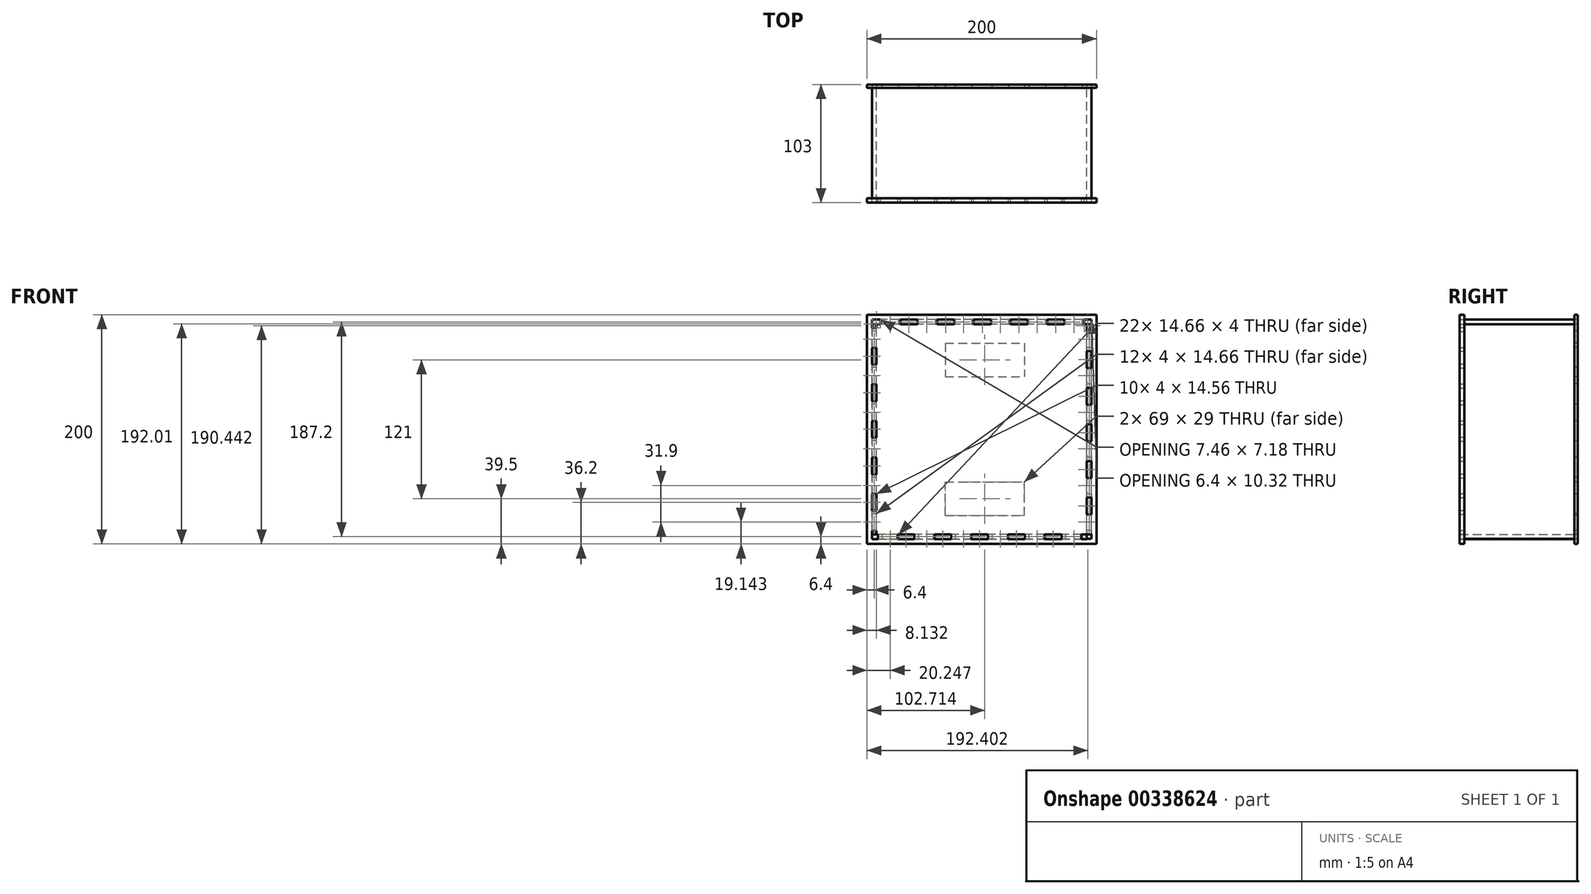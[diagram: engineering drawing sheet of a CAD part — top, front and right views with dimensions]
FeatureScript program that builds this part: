
annotation { "Feature Type Name" : "Feature", "Feature Type Description" : "" }
export const myFeature = defineFeature(function(context is Context, id is Id, definition is map)
    precondition{}
    {
        {
            var Q0;
            Q0=qCreatedBy(makeId("Front.planeOp"),FACE);
            var sketch = newSketch(context, id + "F0", { "sketchPlane" : qUnion([Q0])});
            skLineSegment(sketch, "E0.bottom", {"start": v(-100, 100) * mm, "end": v(100, 100) * mm});
            skLineSegment(sketch, "E0.top", {"start": v(-100, -100) * mm, "end": v(100, -100) * mm});
            skLineSegment(sketch, "E0.left", {"start": v(-100, 100) * mm, "end": v(-100, -100) * mm});
            skLineSegment(sketch, "E0.right", {"start": v(100, 100) * mm, "end": v(100, -100) * mm});
            skPoint(sketch, "E0.middle", {"position": v(0, 0) * mm});
            skSolve(sketch);
        }
        {
            var Q0;
            Q0 = qSketchRegion(id + "F0", true);
            extrude(context, id + "F1", {"entities" : qUnion([Q0]), "depth" : 3 * mm, "offsetDistance" : 25 * mm});
        }
        {
            var Q0;
            Q0=makeQuery(id+"F1.opExtrude","CAP_FACE",FACE,{"disambiguationData":[OSD([sQuery(id+"F0.wireOp",EDGE,"E0.bottom"),sQuery(id+"F0.wireOp",EDGE,"E0.top"),sQuery(id+"F0.wireOp",EDGE,"E0.left"),sQuery(id+"F0.wireOp",EDGE,"E0.right")])],"isStart":false});
            var sketch = newSketch(context, id + "F2", { "sketchPlane" : qUnion([Q0])});
            skLineSegment(sketch, "E1.0", {"start": v(-91.6, 91.6) * mm, "end": v(91.6, 91.6) * mm, "construction": true});
            skLineSegment(sketch, "E1.1", {"start": v(-91.6, 91.6) * mm, "end": v(-91.6, -91.6) * mm, "construction": true});
            skLineSegment(sketch, "E1.2", {"start": v(-91.6, -91.6) * mm, "end": v(91.6, -91.6) * mm, "construction": true});
            skLineSegment(sketch, "E1.3", {"start": v(91.6, 91.6) * mm, "end": v(91.6, -91.6) * mm, "construction": true});
            skLineSegment(sketch, "E2.bottom", {"start": v(-87.08, 95.6) * mm, "end": v(-72.42, 95.6) * mm});
            skLineSegment(sketch, "E2.top", {"start": v(-87.08, 91.6) * mm, "end": v(-72.42, 91.6) * mm});
            skLineSegment(sketch, "E2.left", {"start": v(-87.08, 95.6) * mm, "end": v(-87.08, 91.6) * mm});
            skLineSegment(sketch, "E2.right", {"start": v(-72.42, 95.6) * mm, "end": v(-72.42, 91.6) * mm});
            skLineSegment(sketch, "E3.1.0.0", {"start": v(-55.08, 95.6) * mm, "end": v(-40.42, 95.6) * mm});
            skLineSegment(sketch, "E3.1.0.1", {"start": v(-55.08, 95.6) * mm, "end": v(-55.08, 91.6) * mm});
            skLineSegment(sketch, "E3.1.0.2", {"start": v(-40.42, 95.6) * mm, "end": v(-40.42, 91.6) * mm});
            skLineSegment(sketch, "E3.1.0.3", {"start": v(-55.08, 91.6) * mm, "end": v(-40.42, 91.6) * mm});
            skLineSegment(sketch, "E3.2.0.0", {"start": v(-23.08, 95.6) * mm, "end": v(-8.42, 95.6) * mm});
            skLineSegment(sketch, "E3.2.0.1", {"start": v(-23.08, 95.6) * mm, "end": v(-23.08, 91.6) * mm});
            skLineSegment(sketch, "E3.2.0.2", {"start": v(-8.42, 95.6) * mm, "end": v(-8.42, 91.6) * mm});
            skLineSegment(sketch, "E3.2.0.3", {"start": v(-23.08, 91.6) * mm, "end": v(-8.42, 91.6) * mm});
            skLineSegment(sketch, "E3.3.0.0", {"start": v(8.92, 95.6) * mm, "end": v(23.58, 95.6) * mm});
            skLineSegment(sketch, "E3.3.0.1", {"start": v(8.92, 95.6) * mm, "end": v(8.92, 91.6) * mm});
            skLineSegment(sketch, "E3.3.0.2", {"start": v(23.58, 95.6) * mm, "end": v(23.58, 91.6) * mm});
            skLineSegment(sketch, "E3.3.0.3", {"start": v(8.92, 91.6) * mm, "end": v(23.58, 91.6) * mm});
            skLineSegment(sketch, "E3.4.0.0", {"start": v(40.92, 95.6) * mm, "end": v(55.58, 95.6) * mm});
            skLineSegment(sketch, "E3.4.0.1", {"start": v(40.92, 95.6) * mm, "end": v(40.92, 91.6) * mm});
            skLineSegment(sketch, "E3.4.0.2", {"start": v(55.58, 95.6) * mm, "end": v(55.58, 91.6) * mm});
            skLineSegment(sketch, "E3.4.0.3", {"start": v(40.92, 91.6) * mm, "end": v(55.58, 91.6) * mm});
            skLineSegment(sketch, "E3.5.0.0", {"start": v(72.92, 95.6) * mm, "end": v(87.58, 95.6) * mm});
            skLineSegment(sketch, "E3.5.0.1", {"start": v(72.92, 95.6) * mm, "end": v(72.92, 91.6) * mm});
            skLineSegment(sketch, "E3.5.0.2", {"start": v(87.58, 95.6) * mm, "end": v(87.58, 91.6) * mm});
            skLineSegment(sketch, "E3.5.0.3", {"start": v(72.92, 91.6) * mm, "end": v(87.58, 91.6) * mm});
            skLineSegment(sketch, "E3.direction1", {"start": v(-87.08, 95.6) * mm, "end": v(-55.08, 95.6) * mm, "construction": true});
            skLineSegment(sketch, "E4", {"start": v(0, 100) * mm, "end": v(0, -100) * mm, "construction": true});
            skLineSegment(sketch, "E5", {"start": v(-100, 0) * mm, "end": v(100, 0) * mm, "construction": true});
            skLineSegment(sketch, "E6.MirrorCS", {"start": v(-87.08, -95.6) * mm, "end": v(-87.08, -91.6) * mm});
            skLineSegment(sketch, "E7.MirrorCS", {"start": v(-72.42, -95.6) * mm, "end": v(-72.42, -91.6) * mm});
            skLineSegment(sketch, "E8.MirrorCS", {"start": v(-87.08, -95.6) * mm, "end": v(-72.42, -95.6) * mm});
            skLineSegment(sketch, "E9.MirrorCS", {"start": v(-87.08, -91.6) * mm, "end": v(-72.42, -91.6) * mm});
            skLineSegment(sketch, "E10.MirrorCS", {"start": v(-55.08, -95.6) * mm, "end": v(-40.42, -95.6) * mm});
            skLineSegment(sketch, "E11.MirrorCS", {"start": v(-40.42, -95.6) * mm, "end": v(-40.42, -91.6) * mm});
            skLineSegment(sketch, "E12.MirrorCS", {"start": v(-55.08, -95.6) * mm, "end": v(-55.08, -91.6) * mm});
            skLineSegment(sketch, "E13.MirrorCS", {"start": v(-55.08, -91.6) * mm, "end": v(-40.42, -91.6) * mm});
            skLineSegment(sketch, "E14.MirrorCS", {"start": v(-23.08, -95.6) * mm, "end": v(-8.42, -95.6) * mm});
            skLineSegment(sketch, "E15.MirrorCS", {"start": v(-23.08, -95.6) * mm, "end": v(-23.08, -91.6) * mm});
            skLineSegment(sketch, "E16.MirrorCS", {"start": v(-8.42, -95.6) * mm, "end": v(-8.42, -91.6) * mm});
            skLineSegment(sketch, "E17.MirrorCS", {"start": v(-23.08, -91.6) * mm, "end": v(-8.42, -91.6) * mm});
            skLineSegment(sketch, "E18.MirrorCS", {"start": v(8.92, -95.6) * mm, "end": v(23.58, -95.6) * mm});
            skLineSegment(sketch, "E19.MirrorCS", {"start": v(8.92, -95.6) * mm, "end": v(8.92, -91.6) * mm});
            skLineSegment(sketch, "E20.MirrorCS", {"start": v(23.58, -95.6) * mm, "end": v(23.58, -91.6) * mm});
            skLineSegment(sketch, "E21.MirrorCS", {"start": v(8.92, -91.6) * mm, "end": v(23.58, -91.6) * mm});
            skLineSegment(sketch, "E22.MirrorCS", {"start": v(40.92, -95.6) * mm, "end": v(55.58, -95.6) * mm});
            skLineSegment(sketch, "E23.MirrorCS", {"start": v(40.92, -95.6) * mm, "end": v(40.92, -91.6) * mm});
            skLineSegment(sketch, "E24.MirrorCS", {"start": v(55.58, -95.6) * mm, "end": v(55.58, -91.6) * mm});
            skLineSegment(sketch, "E25.MirrorCS", {"start": v(40.92, -91.6) * mm, "end": v(55.58, -91.6) * mm});
            skLineSegment(sketch, "E26.MirrorCS", {"start": v(72.92, -95.6) * mm, "end": v(87.58, -95.6) * mm});
            skLineSegment(sketch, "E27.MirrorCS", {"start": v(72.92, -95.6) * mm, "end": v(72.92, -91.6) * mm});
            skLineSegment(sketch, "E28.MirrorCS", {"start": v(87.58, -95.6) * mm, "end": v(87.58, -91.6) * mm});
            skLineSegment(sketch, "E29.MirrorCS", {"start": v(72.92, -91.6) * mm, "end": v(87.58, -91.6) * mm});
            skLineSegment(sketch, "E30.bottom", {"start": v(91.6, 85.97) * mm, "end": v(95.6, 85.97) * mm});
            skLineSegment(sketch, "E30.top", {"start": v(91.6, 71.31) * mm, "end": v(95.6, 71.31) * mm});
            skLineSegment(sketch, "E30.left", {"start": v(91.6, 85.97) * mm, "end": v(91.6, 71.31) * mm});
            skLineSegment(sketch, "E30.right", {"start": v(95.6, 85.97) * mm, "end": v(95.6, 71.31) * mm});
            skLineSegment(sketch, "E31.1.0.0", {"start": v(91.6, 54.07) * mm, "end": v(95.6, 54.07) * mm});
            skLineSegment(sketch, "E31.1.0.1", {"start": v(91.6, 39.41) * mm, "end": v(95.6, 39.41) * mm});
            skLineSegment(sketch, "E31.1.0.2", {"start": v(95.6, 54.07) * mm, "end": v(95.6, 39.41) * mm});
            skLineSegment(sketch, "E31.1.0.3", {"start": v(91.6, 54.07) * mm, "end": v(91.6, 39.41) * mm});
            skLineSegment(sketch, "E31.2.0.0", {"start": v(91.6, 22.17) * mm, "end": v(95.6, 22.17) * mm});
            skLineSegment(sketch, "E31.2.0.1", {"start": v(91.6, 7.51) * mm, "end": v(95.6, 7.51) * mm});
            skLineSegment(sketch, "E31.2.0.2", {"start": v(95.6, 22.17) * mm, "end": v(95.6, 7.51) * mm});
            skLineSegment(sketch, "E31.2.0.3", {"start": v(91.6, 22.17) * mm, "end": v(91.6, 7.51) * mm});
            skLineSegment(sketch, "E31.3.0.0", {"start": v(91.6, -9.73) * mm, "end": v(95.6, -9.73) * mm});
            skLineSegment(sketch, "E31.3.0.1", {"start": v(91.6, -24.39) * mm, "end": v(95.6, -24.39) * mm});
            skLineSegment(sketch, "E31.3.0.2", {"start": v(95.6, -9.73) * mm, "end": v(95.6, -24.39) * mm});
            skLineSegment(sketch, "E31.3.0.3", {"start": v(91.6, -9.73) * mm, "end": v(91.6, -24.39) * mm});
            skLineSegment(sketch, "E31.4.0.0", {"start": v(91.6, -41.63) * mm, "end": v(95.6, -41.63) * mm});
            skLineSegment(sketch, "E31.4.0.1", {"start": v(91.6, -56.29) * mm, "end": v(95.6, -56.29) * mm});
            skLineSegment(sketch, "E31.4.0.2", {"start": v(95.6, -41.63) * mm, "end": v(95.6, -56.29) * mm});
            skLineSegment(sketch, "E31.4.0.3", {"start": v(91.6, -41.63) * mm, "end": v(91.6, -56.29) * mm});
            skLineSegment(sketch, "E31.5.0.0", {"start": v(91.6, -73.53) * mm, "end": v(95.6, -73.53) * mm});
            skLineSegment(sketch, "E31.5.0.1", {"start": v(91.6, -88.19) * mm, "end": v(95.6, -88.19) * mm});
            skLineSegment(sketch, "E31.5.0.2", {"start": v(95.6, -73.53) * mm, "end": v(95.6, -88.19) * mm});
            skLineSegment(sketch, "E31.5.0.3", {"start": v(91.6, -73.53) * mm, "end": v(91.6, -88.19) * mm});
            skLineSegment(sketch, "E31.direction1", {"start": v(91.6, 85.97) * mm, "end": v(91.6, 54.07) * mm, "construction": true});
            skLineSegment(sketch, "E32.MirrorCS", {"start": v(-91.6, 85.97) * mm, "end": v(-95.6, 85.97) * mm});
            skLineSegment(sketch, "E33.MirrorCS", {"start": v(-95.6, 85.97) * mm, "end": v(-95.6, 71.31) * mm});
            skLineSegment(sketch, "E34.MirrorCS", {"start": v(-91.6, 71.31) * mm, "end": v(-95.6, 71.31) * mm});
            skLineSegment(sketch, "E35.MirrorCS", {"start": v(-91.6, 85.97) * mm, "end": v(-91.6, 71.31) * mm});
            skLineSegment(sketch, "E36.MirrorCS", {"start": v(-95.6, 54.07) * mm, "end": v(-95.6, 39.41) * mm});
            skLineSegment(sketch, "E37.MirrorCS", {"start": v(-91.6, 54.07) * mm, "end": v(-95.6, 54.07) * mm});
            skLineSegment(sketch, "E38.MirrorCS", {"start": v(-91.6, 39.41) * mm, "end": v(-95.6, 39.41) * mm});
            skLineSegment(sketch, "E39.MirrorCS", {"start": v(-91.6, 54.07) * mm, "end": v(-91.6, 39.41) * mm});
            skLineSegment(sketch, "E40.MirrorCS", {"start": v(-95.6, 22.17) * mm, "end": v(-95.6, 7.51) * mm});
            skLineSegment(sketch, "E41.MirrorCS", {"start": v(-91.6, 22.17) * mm, "end": v(-95.6, 22.17) * mm});
            skLineSegment(sketch, "E42.MirrorCS", {"start": v(-91.6, 7.51) * mm, "end": v(-95.6, 7.51) * mm});
            skLineSegment(sketch, "E43.MirrorCS", {"start": v(-91.6, 22.17) * mm, "end": v(-91.6, 7.51) * mm});
            skLineSegment(sketch, "E44.MirrorCS", {"start": v(-95.6, -9.73) * mm, "end": v(-95.6, -24.39) * mm});
            skLineSegment(sketch, "E45.MirrorCS", {"start": v(-91.6, -9.73) * mm, "end": v(-95.6, -9.73) * mm});
            skLineSegment(sketch, "E46.MirrorCS", {"start": v(-91.6, -9.73) * mm, "end": v(-91.6, -24.39) * mm});
            skLineSegment(sketch, "E47.MirrorCS", {"start": v(-91.6, -24.39) * mm, "end": v(-95.6, -24.39) * mm});
            skLineSegment(sketch, "E48.MirrorCS", {"start": v(-95.6, -41.63) * mm, "end": v(-95.6, -56.29) * mm});
            skLineSegment(sketch, "E49.MirrorCS", {"start": v(-91.6, -41.63) * mm, "end": v(-95.6, -41.63) * mm});
            skLineSegment(sketch, "E50.MirrorCS", {"start": v(-91.6, -56.29) * mm, "end": v(-95.6, -56.29) * mm});
            skLineSegment(sketch, "E51.MirrorCS", {"start": v(-91.6, -41.63) * mm, "end": v(-91.6, -56.29) * mm});
            skLineSegment(sketch, "E52.MirrorCS", {"start": v(-95.6, -73.53) * mm, "end": v(-95.6, -88.19) * mm});
            skLineSegment(sketch, "E53.MirrorCS", {"start": v(-91.6, -73.53) * mm, "end": v(-95.6, -73.53) * mm});
            skLineSegment(sketch, "E54.MirrorCS", {"start": v(-91.6, -88.19) * mm, "end": v(-95.6, -88.19) * mm});
            skLineSegment(sketch, "E55.MirrorCS", {"start": v(-91.6, -73.53) * mm, "end": v(-91.6, -88.19) * mm});
            skSolve(sketch);
        }
        {
            var Q0;
            Q0 = qSketchRegion(id + "F2", true);
            var Q1;
            Q1=makeQuery(id+"F1.opExtrude","CAP_FACE",FACE,{"disambiguationData":[OSD([sQuery(id+"F0.wireOp",EDGE,"E0.bottom"),sQuery(id+"F0.wireOp",EDGE,"E0.top"),sQuery(id+"F0.wireOp",EDGE,"E0.left"),sQuery(id+"F0.wireOp",EDGE,"E0.right")])],"isStart":true});
            extrude(context, id + "F3", {"entities" : qUnion([Q0]), "operationType" : NewBodyOperationType.REMOVE, "endBound" : BoundingType.UP_TO_SURFACE, "oppositeDirection" : true, "depth" : 25 * mm, "endBoundEntityFace" : qUnion([Q1]), "offsetDistance" : 25 * mm});
        }
        {
            var Q0;
            Q0=makeQuery(id+"F1.opExtrude","CAP_FACE",FACE,{"disambiguationData":[OSD([sQuery(id+"F0.wireOp",EDGE,"E0.bottom"),sQuery(id+"F0.wireOp",EDGE,"E0.top"),sQuery(id+"F0.wireOp",EDGE,"E0.left"),sQuery(id+"F0.wireOp",EDGE,"E0.right")])],"isStart":false});
            var sketch = newSketch(context, id + "F4", { "sketchPlane" : qUnion([Q0])});
            skLineSegment(sketch, "E56.0", {"start": v(-87.08, 95.6) * mm, "end": v(-72.42, 95.6) * mm});
            skLineSegment(sketch, "E57.0", {"start": v(-87.08, 95.6) * mm, "end": v(-87.08, 91.6) * mm});
            skLineSegment(sketch, "E58.0", {"start": v(-87.08, 91.6) * mm, "end": v(-72.42, 91.6) * mm});
            skLineSegment(sketch, "E59.0", {"start": v(-72.42, 95.6) * mm, "end": v(-72.42, 91.6) * mm});
            skLineSegment(sketch, "E60.0", {"start": v(-55.08, 95.6) * mm, "end": v(-40.42, 95.6) * mm});
            skLineSegment(sketch, "E61.0", {"start": v(-55.08, 95.6) * mm, "end": v(-55.08, 91.6) * mm});
            skLineSegment(sketch, "E62.0", {"start": v(-55.08, 91.6) * mm, "end": v(-40.42, 91.6) * mm});
            skLineSegment(sketch, "E63.0", {"start": v(-40.42, 95.6) * mm, "end": v(-40.42, 91.6) * mm});
            skLineSegment(sketch, "E64.0", {"start": v(-23.08, 95.6) * mm, "end": v(-8.42, 95.6) * mm});
            skLineSegment(sketch, "E65.0", {"start": v(-23.08, 95.6) * mm, "end": v(-23.08, 91.6) * mm});
            skLineSegment(sketch, "E66.0", {"start": v(-23.08, 91.6) * mm, "end": v(-8.42, 91.6) * mm});
            skLineSegment(sketch, "E67.0", {"start": v(-8.42, 95.6) * mm, "end": v(-8.42, 91.6) * mm});
            skLineSegment(sketch, "E68.0", {"start": v(8.92, 95.6) * mm, "end": v(23.58, 95.6) * mm});
            skLineSegment(sketch, "E69.0", {"start": v(8.92, 95.6) * mm, "end": v(8.92, 91.6) * mm});
            skLineSegment(sketch, "E70.0", {"start": v(8.92, 91.6) * mm, "end": v(23.58, 91.6) * mm});
            skLineSegment(sketch, "E71.0", {"start": v(23.58, 95.6) * mm, "end": v(23.58, 91.6) * mm});
            skLineSegment(sketch, "E72.0", {"start": v(40.92, 95.6) * mm, "end": v(55.58, 95.6) * mm});
            skLineSegment(sketch, "E73.0", {"start": v(40.92, 95.6) * mm, "end": v(40.92, 91.6) * mm});
            skLineSegment(sketch, "E74.0", {"start": v(40.92, 91.6) * mm, "end": v(55.58, 91.6) * mm});
            skLineSegment(sketch, "E75.0", {"start": v(55.58, 95.6) * mm, "end": v(55.58, 91.6) * mm});
            skLineSegment(sketch, "E76.0", {"start": v(72.92, 95.6) * mm, "end": v(87.58, 95.6) * mm});
            skLineSegment(sketch, "E77.0", {"start": v(72.92, 95.6) * mm, "end": v(72.92, 91.6) * mm});
            skLineSegment(sketch, "E78.0", {"start": v(72.92, 91.6) * mm, "end": v(87.58, 91.6) * mm});
            skLineSegment(sketch, "E79.0", {"start": v(87.58, 95.6) * mm, "end": v(87.58, 91.6) * mm});
            skSolve(sketch);
        }
        {
            var Q0;
            Q0 = qSketchRegion(id + "F4", true);
            var Q1;
            Q1=makeQuery(id+"F1.opExtrude","CAP_FACE",FACE,{"disambiguationData":[OSD([sQuery(id+"F0.wireOp",EDGE,"E0.bottom"),sQuery(id+"F0.wireOp",EDGE,"E0.top"),sQuery(id+"F0.wireOp",EDGE,"E0.left"),sQuery(id+"F0.wireOp",EDGE,"E0.right")])],"isStart":true});
            extrude(context, id + "F5", {"entities" : qUnion([Q0]), "endBound" : BoundingType.UP_TO_SURFACE, "oppositeDirection" : true, "depth" : 25 * mm, "endBoundEntityFace" : qUnion([Q1]), "offsetDistance" : 25 * mm});
        }
        {
            var Q0;
            Q0=makeQuery(id+"F1.opExtrude","CAP_FACE",FACE,{"disambiguationData":[OSD([sQuery(id+"F0.wireOp",EDGE,"E0.bottom"),sQuery(id+"F0.wireOp",EDGE,"E0.top"),sQuery(id+"F0.wireOp",EDGE,"E0.left"),sQuery(id+"F0.wireOp",EDGE,"E0.right")])],"isStart":false});
            var sketch = newSketch(context, id + "F6", { "sketchPlane" : qUnion([Q0])});
            skPoint(sketch, "E80.oppositeSnap0", {"position": v(48.25, 91.6) * mm});
            skLineSegment(sketch, "E80.bottom", {"start": v(-95.6, 95.6) * mm, "end": v(95.6, 95.6) * mm});
            skLineSegment(sketch, "E80.top", {"start": v(-95.6, 91.6) * mm, "end": v(95.6, 91.6) * mm});
            skLineSegment(sketch, "E80.left", {"start": v(-95.6, 95.6) * mm, "end": v(-95.6, 91.6) * mm});
            skLineSegment(sketch, "E80.right", {"start": v(95.6, 95.6) * mm, "end": v(95.6, 91.6) * mm});
            skSolve(sketch);
        }
        {
            var Q0;
            Q0 = qSketchRegion(id + "F6", true);
            extrude(context, id + "F7", {"entities" : qUnion([Q0]), "depth" : 100 * mm, "offsetDistance" : 25 * mm});
        }
        {
            var Q0;
            Q0=makeQuery(id+"F5.opExtrude","SWEPT_BODY",BODY,{"disambiguationData":[OSD([sQuery(id+"F4.wireOp",EDGE,"E56.0"),sQuery(id+"F4.wireOp",EDGE,"E57.0"),sQuery(id+"F4.wireOp",EDGE,"E58.0"),sQuery(id+"F4.wireOp",EDGE,"E59.0")])]});
            var Q1;
            Q1=makeQuery(id+"F5.opExtrude","SWEPT_BODY",BODY,{"disambiguationData":[OSD([sQuery(id+"F4.wireOp",EDGE,"E60.0"),sQuery(id+"F4.wireOp",EDGE,"E61.0"),sQuery(id+"F4.wireOp",EDGE,"E62.0"),sQuery(id+"F4.wireOp",EDGE,"E63.0")])]});
            var Q2;
            Q2=makeQuery(id+"F5.opExtrude","SWEPT_BODY",BODY,{"disambiguationData":[OSD([sQuery(id+"F4.wireOp",EDGE,"E64.0"),sQuery(id+"F4.wireOp",EDGE,"E65.0"),sQuery(id+"F4.wireOp",EDGE,"E66.0"),sQuery(id+"F4.wireOp",EDGE,"E67.0")])]});
            var Q3;
            Q3=makeQuery(id+"F5.opExtrude","SWEPT_BODY",BODY,{"disambiguationData":[OSD([sQuery(id+"F4.wireOp",EDGE,"E68.0"),sQuery(id+"F4.wireOp",EDGE,"E69.0"),sQuery(id+"F4.wireOp",EDGE,"E70.0"),sQuery(id+"F4.wireOp",EDGE,"E71.0")])]});
            var Q4;
            Q4=makeQuery(id+"F5.opExtrude","SWEPT_BODY",BODY,{"disambiguationData":[OSD([sQuery(id+"F4.wireOp",EDGE,"E72.0"),sQuery(id+"F4.wireOp",EDGE,"E73.0"),sQuery(id+"F4.wireOp",EDGE,"E74.0"),sQuery(id+"F4.wireOp",EDGE,"E75.0")])]});
            var Q5;
            Q5=makeQuery(id+"F5.opExtrude","SWEPT_BODY",BODY,{"disambiguationData":[OSD([sQuery(id+"F4.wireOp",EDGE,"E76.0"),sQuery(id+"F4.wireOp",EDGE,"E77.0"),sQuery(id+"F4.wireOp",EDGE,"E78.0"),sQuery(id+"F4.wireOp",EDGE,"E79.0")])]});
            var Q6;
            Q6=makeQuery(id+"F7.opExtrude","SWEPT_BODY",BODY,{"disambiguationData":[OSD([sQuery(id+"F6.wireOp",EDGE,"E80.bottom"),sQuery(id+"F6.wireOp",EDGE,"E80.top"),sQuery(id+"F6.wireOp",EDGE,"E80.left"),sQuery(id+"F6.wireOp",EDGE,"E80.right")])]});
            booleanBodies(context, id + "F8", {"operationType" : BooleanOperationType.UNION, "tools" : qUnion([Q0, Q1, Q2, Q3, Q4, Q5, Q6])});
        }
        {
            var Q0;
            Q0=makeQuery(id+"F1.opExtrude","CAP_FACE",FACE,{"disambiguationData":[OSD([sQuery(id+"F0.wireOp",EDGE,"E0.bottom"),sQuery(id+"F0.wireOp",EDGE,"E0.top"),sQuery(id+"F0.wireOp",EDGE,"E0.left"),sQuery(id+"F0.wireOp",EDGE,"E0.right")])],"isStart":false});
            var sketch = newSketch(context, id + "F9", { "sketchPlane" : qUnion([Q0])});
            skLineSegment(sketch, "E81.0", {"start": v(95.6, 85.97) * mm, "end": v(95.6, 71.31) * mm});
            skLineSegment(sketch, "E82.0", {"start": v(91.6, 85.97) * mm, "end": v(95.6, 85.97) * mm});
            skLineSegment(sketch, "E83.0", {"start": v(91.6, 85.97) * mm, "end": v(91.6, 71.31) * mm});
            skLineSegment(sketch, "E84.0", {"start": v(91.6, 71.31) * mm, "end": v(95.6, 71.31) * mm});
            skLineSegment(sketch, "E85.0", {"start": v(95.6, 54.07) * mm, "end": v(95.6, 39.41) * mm});
            skLineSegment(sketch, "E86.0", {"start": v(91.6, 54.07) * mm, "end": v(95.6, 54.07) * mm});
            skLineSegment(sketch, "E87.0", {"start": v(91.6, 54.07) * mm, "end": v(91.6, 39.41) * mm});
            skLineSegment(sketch, "E88.0", {"start": v(91.6, 39.41) * mm, "end": v(95.6, 39.41) * mm});
            skLineSegment(sketch, "E89.0", {"start": v(95.6, 22.17) * mm, "end": v(95.6, 7.51) * mm});
            skLineSegment(sketch, "E90.0", {"start": v(91.6, 22.17) * mm, "end": v(95.6, 22.17) * mm});
            skLineSegment(sketch, "E91.0", {"start": v(91.6, 22.17) * mm, "end": v(91.6, 7.51) * mm});
            skLineSegment(sketch, "E92.0", {"start": v(91.6, 7.51) * mm, "end": v(95.6, 7.51) * mm});
            skLineSegment(sketch, "E93.0", {"start": v(95.6, -9.73) * mm, "end": v(95.6, -24.39) * mm});
            skLineSegment(sketch, "E94.0", {"start": v(91.6, -9.73) * mm, "end": v(95.6, -9.73) * mm});
            skLineSegment(sketch, "E95.0", {"start": v(91.6, -9.73) * mm, "end": v(91.6, -24.39) * mm});
            skLineSegment(sketch, "E96.0", {"start": v(91.6, -24.39) * mm, "end": v(95.6, -24.39) * mm});
            skLineSegment(sketch, "E97.0", {"start": v(95.6, -41.63) * mm, "end": v(95.6, -56.29) * mm});
            skLineSegment(sketch, "E98.0", {"start": v(91.6, -41.63) * mm, "end": v(95.6, -41.63) * mm});
            skLineSegment(sketch, "E99.0", {"start": v(91.6, -41.63) * mm, "end": v(91.6, -56.29) * mm});
            skLineSegment(sketch, "E100.0", {"start": v(91.6, -56.29) * mm, "end": v(95.6, -56.29) * mm});
            skLineSegment(sketch, "E101.0", {"start": v(95.6, -73.53) * mm, "end": v(95.6, -88.19) * mm});
            skLineSegment(sketch, "E102.0", {"start": v(91.6, -73.53) * mm, "end": v(95.6, -73.53) * mm});
            skLineSegment(sketch, "E103.0", {"start": v(91.6, -73.53) * mm, "end": v(91.6, -88.19) * mm});
            skLineSegment(sketch, "E104.0", {"start": v(91.6, -88.19) * mm, "end": v(95.6, -88.19) * mm});
            skSolve(sketch);
        }
        {
            var Q0;
            Q0 = qSketchRegion(id + "F9", true);
            var Q1;
            Q1=makeQuery(id+"F1.opExtrude","CAP_FACE",FACE,{"disambiguationData":[OSD([sQuery(id+"F0.wireOp",EDGE,"E0.bottom"),sQuery(id+"F0.wireOp",EDGE,"E0.top"),sQuery(id+"F0.wireOp",EDGE,"E0.left"),sQuery(id+"F0.wireOp",EDGE,"E0.right")])],"isStart":true});
            extrude(context, id + "F10", {"entities" : qUnion([Q0]), "endBound" : BoundingType.UP_TO_SURFACE, "oppositeDirection" : true, "depth" : 25 * mm, "endBoundEntityFace" : qUnion([Q1]), "offsetDistance" : 25 * mm});
        }
        {
            var Q0;
            Q0=makeQuery(id+"F1.opExtrude","CAP_FACE",FACE,{"disambiguationData":[OSD([sQuery(id+"F0.wireOp",EDGE,"E0.bottom"),sQuery(id+"F0.wireOp",EDGE,"E0.top"),sQuery(id+"F0.wireOp",EDGE,"E0.left"),sQuery(id+"F0.wireOp",EDGE,"E0.right")])],"isStart":false});
            var sketch = newSketch(context, id + "F11", { "sketchPlane" : qUnion([Q0])});
            skPoint(sketch, "E105.oppositeSnap0", {"position": v(91.6, -48.96) * mm});
            skLineSegment(sketch, "E105.bottom", {"start": v(95.6, 91.72) * mm, "end": v(91.6, 91.72) * mm});
            skLineSegment(sketch, "E105.top", {"start": v(95.6, -95.56) * mm, "end": v(91.6, -95.56) * mm});
            skLineSegment(sketch, "E105.left", {"start": v(95.6, 91.72) * mm, "end": v(95.6, -95.56) * mm});
            skLineSegment(sketch, "E105.right", {"start": v(91.6, 91.72) * mm, "end": v(91.6, -95.56) * mm});
            skSolve(sketch);
        }
        {
            var Q0;
            Q0 = qSketchRegion(id + "F11", true);
            extrude(context, id + "F12", {"entities" : qUnion([Q0]), "depth" : 100 * mm, "offsetDistance" : 25 * mm});
        }
        {
            var Q0;
            Q0=makeQuery(id+"F10.opExtrude","SWEPT_BODY",BODY,{"disambiguationData":[OSD([sQuery(id+"F9.wireOp",EDGE,"E81.0"),sQuery(id+"F9.wireOp",EDGE,"E82.0"),sQuery(id+"F9.wireOp",EDGE,"E83.0"),sQuery(id+"F9.wireOp",EDGE,"E84.0")])]});
            var Q1;
            Q1=makeQuery(id+"F10.opExtrude","SWEPT_BODY",BODY,{"disambiguationData":[OSD([sQuery(id+"F9.wireOp",EDGE,"E85.0"),sQuery(id+"F9.wireOp",EDGE,"E86.0"),sQuery(id+"F9.wireOp",EDGE,"E87.0"),sQuery(id+"F9.wireOp",EDGE,"E88.0")])]});
            var Q2;
            Q2=makeQuery(id+"F10.opExtrude","SWEPT_BODY",BODY,{"disambiguationData":[OSD([sQuery(id+"F9.wireOp",EDGE,"E89.0"),sQuery(id+"F9.wireOp",EDGE,"E90.0"),sQuery(id+"F9.wireOp",EDGE,"E91.0"),sQuery(id+"F9.wireOp",EDGE,"E92.0")])]});
            var Q3;
            Q3=makeQuery(id+"F10.opExtrude","SWEPT_BODY",BODY,{"disambiguationData":[OSD([sQuery(id+"F9.wireOp",EDGE,"E93.0"),sQuery(id+"F9.wireOp",EDGE,"E94.0"),sQuery(id+"F9.wireOp",EDGE,"E95.0"),sQuery(id+"F9.wireOp",EDGE,"E96.0")])]});
            var Q4;
            Q4=makeQuery(id+"F10.opExtrude","SWEPT_BODY",BODY,{"disambiguationData":[OSD([sQuery(id+"F9.wireOp",EDGE,"E97.0"),sQuery(id+"F9.wireOp",EDGE,"E98.0"),sQuery(id+"F9.wireOp",EDGE,"E99.0"),sQuery(id+"F9.wireOp",EDGE,"E100.0")])]});
            var Q5;
            Q5=makeQuery(id+"F10.opExtrude","SWEPT_BODY",BODY,{"disambiguationData":[OSD([sQuery(id+"F9.wireOp",EDGE,"E101.0"),sQuery(id+"F9.wireOp",EDGE,"E102.0"),sQuery(id+"F9.wireOp",EDGE,"E103.0"),sQuery(id+"F9.wireOp",EDGE,"E104.0")])]});
            var Q6;
            Q6=makeQuery(id+"F12.opExtrude","SWEPT_BODY",BODY,{"disambiguationData":[OSD([sQuery(id+"F11.wireOp",EDGE,"E105.bottom"),sQuery(id+"F11.wireOp",EDGE,"E105.top"),sQuery(id+"F11.wireOp",EDGE,"E105.left"),sQuery(id+"F11.wireOp",EDGE,"E105.right")])]});
            booleanBodies(context, id + "F13", {"operationType" : BooleanOperationType.UNION, "tools" : qUnion([Q0, Q1, Q2, Q3, Q4, Q5, Q6])});
        }
        {
            var Q0;
            Q0=makeQuery(id+"F1.opExtrude","CAP_FACE",FACE,{"disambiguationData":[OSD([sQuery(id+"F0.wireOp",EDGE,"E0.bottom"),sQuery(id+"F0.wireOp",EDGE,"E0.top"),sQuery(id+"F0.wireOp",EDGE,"E0.left"),sQuery(id+"F0.wireOp",EDGE,"E0.right")])],"isStart":false});
            var sketch = newSketch(context, id + "F14", { "sketchPlane" : qUnion([Q0])});
            skLineSegment(sketch, "E106.0", {"start": v(72.92, -95.6) * mm, "end": v(87.58, -95.6) * mm});
            skLineSegment(sketch, "E107.0", {"start": v(87.58, -95.6) * mm, "end": v(87.58, -91.6) * mm});
            skLineSegment(sketch, "E108.0", {"start": v(72.92, -91.6) * mm, "end": v(87.58, -91.6) * mm});
            skLineSegment(sketch, "E109.0", {"start": v(72.92, -95.6) * mm, "end": v(72.92, -91.6) * mm});
            skLineSegment(sketch, "E110.0", {"start": v(40.92, -95.6) * mm, "end": v(55.58, -95.6) * mm});
            skLineSegment(sketch, "E111.0", {"start": v(55.58, -95.6) * mm, "end": v(55.58, -91.6) * mm});
            skLineSegment(sketch, "E112.0", {"start": v(40.92, -91.6) * mm, "end": v(55.58, -91.6) * mm});
            skLineSegment(sketch, "E113.0", {"start": v(40.92, -95.6) * mm, "end": v(40.92, -91.6) * mm});
            skLineSegment(sketch, "E114.0", {"start": v(8.92, -95.6) * mm, "end": v(23.58, -95.6) * mm});
            skLineSegment(sketch, "E115.0", {"start": v(23.58, -95.6) * mm, "end": v(23.58, -91.6) * mm});
            skLineSegment(sketch, "E116.0", {"start": v(8.92, -91.6) * mm, "end": v(23.58, -91.6) * mm});
            skLineSegment(sketch, "E117.0", {"start": v(8.92, -95.6) * mm, "end": v(8.92, -91.6) * mm});
            skLineSegment(sketch, "E118.0", {"start": v(-23.08, -95.6) * mm, "end": v(-8.42, -95.6) * mm});
            skLineSegment(sketch, "E119.0", {"start": v(-8.42, -95.6) * mm, "end": v(-8.42, -91.6) * mm});
            skLineSegment(sketch, "E120.0", {"start": v(-23.08, -91.6) * mm, "end": v(-8.42, -91.6) * mm});
            skLineSegment(sketch, "E121.0", {"start": v(-23.08, -95.6) * mm, "end": v(-23.08, -91.6) * mm});
            skLineSegment(sketch, "E122.0", {"start": v(-55.08, -95.6) * mm, "end": v(-40.42, -95.6) * mm});
            skLineSegment(sketch, "E123.0", {"start": v(-40.42, -95.6) * mm, "end": v(-40.42, -91.6) * mm});
            skLineSegment(sketch, "E124.0", {"start": v(-55.08, -91.6) * mm, "end": v(-40.42, -91.6) * mm});
            skLineSegment(sketch, "E125.0", {"start": v(-55.08, -95.6) * mm, "end": v(-55.08, -91.6) * mm});
            skLineSegment(sketch, "E126.0", {"start": v(-87.08, -95.6) * mm, "end": v(-72.42, -95.6) * mm});
            skLineSegment(sketch, "E127.0", {"start": v(-72.42, -95.6) * mm, "end": v(-72.42, -91.6) * mm});
            skLineSegment(sketch, "E128.0", {"start": v(-87.08, -91.6) * mm, "end": v(-72.42, -91.6) * mm});
            skLineSegment(sketch, "E129.0", {"start": v(-87.08, -95.6) * mm, "end": v(-87.08, -91.6) * mm});
            skSolve(sketch);
        }
        {
            var Q0;
            Q0 = qSketchRegion(id + "F14", true);
            var Q1;
            Q1=makeQuery(id+"F1.opExtrude","CAP_FACE",FACE,{"disambiguationData":[OSD([sQuery(id+"F0.wireOp",EDGE,"E0.bottom"),sQuery(id+"F0.wireOp",EDGE,"E0.top"),sQuery(id+"F0.wireOp",EDGE,"E0.left"),sQuery(id+"F0.wireOp",EDGE,"E0.right")])],"isStart":true});
            extrude(context, id + "F15", {"entities" : qUnion([Q0]), "endBound" : BoundingType.UP_TO_SURFACE, "oppositeDirection" : true, "depth" : 25 * mm, "endBoundEntityFace" : qUnion([Q1]), "offsetDistance" : 25 * mm});
        }
        {
            var Q0;
            Q0=makeQuery(id+"F1.opExtrude","CAP_FACE",FACE,{"disambiguationData":[OSD([sQuery(id+"F0.wireOp",EDGE,"E0.bottom"),sQuery(id+"F0.wireOp",EDGE,"E0.top"),sQuery(id+"F0.wireOp",EDGE,"E0.left"),sQuery(id+"F0.wireOp",EDGE,"E0.right")])],"isStart":false});
            var sketch = newSketch(context, id + "F16", { "sketchPlane" : qUnion([Q0])});
            skLineSegment(sketch, "E130.bottom", {"start": v(91.53, -95.6) * mm, "end": v(-95.49, -95.6) * mm});
            skLineSegment(sketch, "E130.top", {"start": v(91.53, -91.6) * mm, "end": v(-95.49, -91.6) * mm});
            skLineSegment(sketch, "E130.left", {"start": v(91.53, -95.6) * mm, "end": v(91.53, -91.6) * mm});
            skLineSegment(sketch, "E130.right", {"start": v(-95.49, -95.6) * mm, "end": v(-95.49, -91.6) * mm});
            skSolve(sketch);
        }
        {
            var Q0;
            Q0 = qSketchRegion(id + "F16", true);
            extrude(context, id + "F17", {"entities" : qUnion([Q0]), "depth" : 100 * mm, "offsetDistance" : 25 * mm});
        }
        {
            var Q0;
            Q0=makeQuery(id+"F15.opExtrude","SWEPT_BODY",BODY,{"disambiguationData":[OSD([sQuery(id+"F14.wireOp",EDGE,"E106.0"),sQuery(id+"F14.wireOp",EDGE,"E107.0"),sQuery(id+"F14.wireOp",EDGE,"E108.0"),sQuery(id+"F14.wireOp",EDGE,"E109.0")])]});
            var Q1;
            Q1=makeQuery(id+"F15.opExtrude","SWEPT_BODY",BODY,{"disambiguationData":[OSD([sQuery(id+"F14.wireOp",EDGE,"E110.0"),sQuery(id+"F14.wireOp",EDGE,"E111.0"),sQuery(id+"F14.wireOp",EDGE,"E112.0"),sQuery(id+"F14.wireOp",EDGE,"E113.0")])]});
            var Q2;
            Q2=makeQuery(id+"F15.opExtrude","SWEPT_BODY",BODY,{"disambiguationData":[OSD([sQuery(id+"F14.wireOp",EDGE,"E114.0"),sQuery(id+"F14.wireOp",EDGE,"E115.0"),sQuery(id+"F14.wireOp",EDGE,"E116.0"),sQuery(id+"F14.wireOp",EDGE,"E117.0")])]});
            var Q3;
            Q3=makeQuery(id+"F15.opExtrude","SWEPT_BODY",BODY,{"disambiguationData":[OSD([sQuery(id+"F14.wireOp",EDGE,"E118.0"),sQuery(id+"F14.wireOp",EDGE,"E119.0"),sQuery(id+"F14.wireOp",EDGE,"E120.0"),sQuery(id+"F14.wireOp",EDGE,"E121.0")])]});
            var Q4;
            Q4=makeQuery(id+"F15.opExtrude","SWEPT_BODY",BODY,{"disambiguationData":[OSD([sQuery(id+"F14.wireOp",EDGE,"E122.0"),sQuery(id+"F14.wireOp",EDGE,"E123.0"),sQuery(id+"F14.wireOp",EDGE,"E124.0"),sQuery(id+"F14.wireOp",EDGE,"E125.0")])]});
            var Q5;
            Q5=makeQuery(id+"F15.opExtrude","SWEPT_BODY",BODY,{"disambiguationData":[OSD([sQuery(id+"F14.wireOp",EDGE,"E126.0"),sQuery(id+"F14.wireOp",EDGE,"E127.0"),sQuery(id+"F14.wireOp",EDGE,"E128.0"),sQuery(id+"F14.wireOp",EDGE,"E129.0")])]});
            var Q6;
            Q6=makeQuery(id+"F17.opExtrude","SWEPT_BODY",BODY,{"disambiguationData":[OSD([sQuery(id+"F16.wireOp",EDGE,"E130.bottom"),sQuery(id+"F16.wireOp",EDGE,"E130.top"),sQuery(id+"F16.wireOp",EDGE,"E130.left"),sQuery(id+"F16.wireOp",EDGE,"E130.right")])]});
            booleanBodies(context, id + "F18", {"operationType" : BooleanOperationType.UNION, "tools" : qUnion([Q0, Q1, Q2, Q3, Q4, Q5, Q6])});
        }
        {
            var Q0;
            Q0=makeQuery(id+"F1.opExtrude","CAP_FACE",FACE,{"disambiguationData":[OSD([sQuery(id+"F0.wireOp",EDGE,"E0.bottom"),sQuery(id+"F0.wireOp",EDGE,"E0.top"),sQuery(id+"F0.wireOp",EDGE,"E0.left"),sQuery(id+"F0.wireOp",EDGE,"E0.right")])],"isStart":false});
            var sketch = newSketch(context, id + "F19", { "sketchPlane" : qUnion([Q0])});
            skLineSegment(sketch, "E131.0", {"start": v(-91.6, -88.19) * mm, "end": v(-95.6, -88.19) * mm});
            skLineSegment(sketch, "E132.0", {"start": v(-95.6, -73.53) * mm, "end": v(-95.6, -88.19) * mm});
            skLineSegment(sketch, "E133.0", {"start": v(-91.6, -73.53) * mm, "end": v(-91.6, -88.19) * mm});
            skLineSegment(sketch, "E134.0", {"start": v(-91.6, -73.53) * mm, "end": v(-95.6, -73.53) * mm});
            skLineSegment(sketch, "E135.0", {"start": v(-95.6, -41.63) * mm, "end": v(-95.6, -56.29) * mm});
            skLineSegment(sketch, "E136.0", {"start": v(-91.6, -56.29) * mm, "end": v(-95.6, -56.29) * mm});
            skLineSegment(sketch, "E137.0", {"start": v(-91.6, -41.63) * mm, "end": v(-91.6, -56.29) * mm});
            skLineSegment(sketch, "E138.0", {"start": v(-91.6, -41.63) * mm, "end": v(-95.6, -41.63) * mm});
            skLineSegment(sketch, "E139.0", {"start": v(-95.6, -9.73) * mm, "end": v(-95.6, -24.39) * mm});
            skLineSegment(sketch, "E140.0", {"start": v(-91.6, -24.39) * mm, "end": v(-95.6, -24.39) * mm});
            skLineSegment(sketch, "E141.0", {"start": v(-91.6, -9.73) * mm, "end": v(-91.6, -24.39) * mm});
            skLineSegment(sketch, "E142.0", {"start": v(-91.6, -9.73) * mm, "end": v(-95.6, -9.73) * mm});
            skLineSegment(sketch, "E143.0", {"start": v(-95.6, 22.17) * mm, "end": v(-95.6, 7.51) * mm});
            skLineSegment(sketch, "E144.0", {"start": v(-91.6, 7.51) * mm, "end": v(-95.6, 7.51) * mm});
            skLineSegment(sketch, "E145.0", {"start": v(-91.6, 22.17) * mm, "end": v(-91.6, 7.51) * mm});
            skLineSegment(sketch, "E146.0", {"start": v(-91.6, 22.17) * mm, "end": v(-95.6, 22.17) * mm});
            skLineSegment(sketch, "E147.0", {"start": v(-95.6, 54.07) * mm, "end": v(-95.6, 39.41) * mm});
            skLineSegment(sketch, "E148.0", {"start": v(-91.6, 39.41) * mm, "end": v(-95.6, 39.41) * mm});
            skLineSegment(sketch, "E149.0", {"start": v(-91.6, 54.07) * mm, "end": v(-91.6, 39.41) * mm});
            skLineSegment(sketch, "E150.0", {"start": v(-91.6, 54.07) * mm, "end": v(-95.6, 54.07) * mm});
            skLineSegment(sketch, "E151.0", {"start": v(-95.6, 85.97) * mm, "end": v(-95.6, 71.31) * mm});
            skLineSegment(sketch, "E152.0", {"start": v(-91.6, 71.31) * mm, "end": v(-95.6, 71.31) * mm});
            skLineSegment(sketch, "E153.0", {"start": v(-91.6, 85.97) * mm, "end": v(-91.6, 71.31) * mm});
            skLineSegment(sketch, "E154.0", {"start": v(-91.6, 85.97) * mm, "end": v(-95.6, 85.97) * mm});
            skSolve(sketch);
        }
        {
            var Q0;
            Q0 = qSketchRegion(id + "F19", true);
            var Q1;
            Q1=makeQuery(id+"F1.opExtrude","CAP_FACE",FACE,{"disambiguationData":[OSD([sQuery(id+"F0.wireOp",EDGE,"E0.bottom"),sQuery(id+"F0.wireOp",EDGE,"E0.top"),sQuery(id+"F0.wireOp",EDGE,"E0.left"),sQuery(id+"F0.wireOp",EDGE,"E0.right")])],"isStart":true});
            extrude(context, id + "F20", {"entities" : qUnion([Q0]), "endBound" : BoundingType.UP_TO_SURFACE, "oppositeDirection" : true, "depth" : 25 * mm, "endBoundEntityFace" : qUnion([Q1]), "offsetDistance" : 25 * mm});
        }
        {
            var Q0;
            Q0=makeQuery(id+"F1.opExtrude","CAP_FACE",FACE,{"disambiguationData":[OSD([sQuery(id+"F0.wireOp",EDGE,"E0.bottom"),sQuery(id+"F0.wireOp",EDGE,"E0.top"),sQuery(id+"F0.wireOp",EDGE,"E0.left"),sQuery(id+"F0.wireOp",EDGE,"E0.right")])],"isStart":false});
            var sketch = newSketch(context, id + "F21", { "sketchPlane" : qUnion([Q0])});
            skLineSegment(sketch, "E155.bottom", {"start": v(-95.6, -91.68) * mm, "end": v(-91.6, -91.68) * mm});
            skLineSegment(sketch, "E155.top", {"start": v(-95.6, 91.74) * mm, "end": v(-91.6, 91.74) * mm});
            skLineSegment(sketch, "E155.left", {"start": v(-95.6, -91.68) * mm, "end": v(-95.6, 91.74) * mm});
            skLineSegment(sketch, "E155.right", {"start": v(-91.6, -91.68) * mm, "end": v(-91.6, 91.74) * mm});
            skSolve(sketch);
        }
        {
            var Q0;
            Q0 = qSketchRegion(id + "F21", true);
            extrude(context, id + "F22", {"entities" : qUnion([Q0]), "depth" : 100 * mm, "offsetDistance" : 25 * mm});
        }
        {
            var Q0;
            Q0=makeQuery(id+"F20.opExtrude","SWEPT_BODY",BODY,{"disambiguationData":[OSD([sQuery(id+"F19.wireOp",EDGE,"E131.0"),sQuery(id+"F19.wireOp",EDGE,"E132.0"),sQuery(id+"F19.wireOp",EDGE,"E133.0"),sQuery(id+"F19.wireOp",EDGE,"E134.0")])]});
            var Q1;
            Q1=makeQuery(id+"F20.opExtrude","SWEPT_BODY",BODY,{"disambiguationData":[OSD([sQuery(id+"F19.wireOp",EDGE,"E135.0"),sQuery(id+"F19.wireOp",EDGE,"E136.0"),sQuery(id+"F19.wireOp",EDGE,"E137.0"),sQuery(id+"F19.wireOp",EDGE,"E138.0")])]});
            var Q2;
            Q2=makeQuery(id+"F20.opExtrude","SWEPT_BODY",BODY,{"disambiguationData":[OSD([sQuery(id+"F19.wireOp",EDGE,"E139.0"),sQuery(id+"F19.wireOp",EDGE,"E140.0"),sQuery(id+"F19.wireOp",EDGE,"E141.0"),sQuery(id+"F19.wireOp",EDGE,"E142.0")])]});
            var Q3;
            Q3=makeQuery(id+"F20.opExtrude","SWEPT_BODY",BODY,{"disambiguationData":[OSD([sQuery(id+"F19.wireOp",EDGE,"E143.0"),sQuery(id+"F19.wireOp",EDGE,"E144.0"),sQuery(id+"F19.wireOp",EDGE,"E145.0"),sQuery(id+"F19.wireOp",EDGE,"E146.0")])]});
            var Q4;
            Q4=makeQuery(id+"F20.opExtrude","SWEPT_BODY",BODY,{"disambiguationData":[OSD([sQuery(id+"F19.wireOp",EDGE,"E147.0"),sQuery(id+"F19.wireOp",EDGE,"E148.0"),sQuery(id+"F19.wireOp",EDGE,"E149.0"),sQuery(id+"F19.wireOp",EDGE,"E150.0")])]});
            var Q5;
            Q5=makeQuery(id+"F20.opExtrude","SWEPT_BODY",BODY,{"disambiguationData":[OSD([sQuery(id+"F19.wireOp",EDGE,"E151.0"),sQuery(id+"F19.wireOp",EDGE,"E152.0"),sQuery(id+"F19.wireOp",EDGE,"E153.0"),sQuery(id+"F19.wireOp",EDGE,"E154.0")])]});
            var Q6;
            Q6=makeQuery(id+"F22.opExtrude","SWEPT_BODY",BODY,{"disambiguationData":[OSD([sQuery(id+"F21.wireOp",EDGE,"E155.bottom"),sQuery(id+"F21.wireOp",EDGE,"E155.top"),sQuery(id+"F21.wireOp",EDGE,"E155.left"),sQuery(id+"F21.wireOp",EDGE,"E155.right")])]});
            booleanBodies(context, id + "F23", {"operationType" : BooleanOperationType.UNION, "tools" : qUnion([Q0, Q1, Q2, Q3, Q4, Q5, Q6])});
        }
        {
            var Q0;
            Q0=makeQuery(id+"F1.opExtrude","CAP_FACE",FACE,{"disambiguationData":[OSD([sQuery(id+"F0.wireOp",EDGE,"E0.bottom"),sQuery(id+"F0.wireOp",EDGE,"E0.top"),sQuery(id+"F0.wireOp",EDGE,"E0.left"),sQuery(id+"F0.wireOp",EDGE,"E0.right")])],"isStart":false});
            var sketch = newSketch(context, id + "F24", { "sketchPlane" : qUnion([Q0])});
            skLineSegment(sketch, "E156.bottom", {"start": v(-31.79, -75) * mm, "end": v(37.21, -75) * mm});
            skLineSegment(sketch, "E156.top", {"start": v(-31.79, -46) * mm, "end": v(37.21, -46) * mm});
            skLineSegment(sketch, "E156.left", {"start": v(-31.79, -75) * mm, "end": v(-31.79, -46) * mm});
            skLineSegment(sketch, "E156.right", {"start": v(37.21, -75) * mm, "end": v(37.21, -46) * mm});
            skLineSegment(sketch, "E157", {"start": v(-100, 0) * mm, "end": v(100, 0) * mm, "construction": true});
            skLineSegment(sketch, "E158.MirrorCS", {"start": v(-31.79, 75) * mm, "end": v(-31.79, 46) * mm});
            skLineSegment(sketch, "E159.MirrorCS", {"start": v(-31.79, 46) * mm, "end": v(37.21, 46) * mm});
            skLineSegment(sketch, "E160.MirrorCS", {"start": v(-31.79, 75) * mm, "end": v(37.21, 75) * mm});
            skLineSegment(sketch, "E161.MirrorCS", {"start": v(37.21, 75) * mm, "end": v(37.21, 46) * mm});
            skSolve(sketch);
        }
        {
            var Q0;
            Q0 = qSketchRegion(id + "F24", true);
            var Q1;
            Q1=makeQuery(id+"F1.opExtrude","CAP_FACE",FACE,{"disambiguationData":[OSD([sQuery(id+"F0.wireOp",EDGE,"E0.bottom"),sQuery(id+"F0.wireOp",EDGE,"E0.top"),sQuery(id+"F0.wireOp",EDGE,"E0.left"),sQuery(id+"F0.wireOp",EDGE,"E0.right")])],"isStart":true});
            extrude(context, id + "F25", {"entities" : qUnion([Q0]), "operationType" : NewBodyOperationType.REMOVE, "endBound" : BoundingType.UP_TO_SURFACE, "oppositeDirection" : true, "depth" : 25 * mm, "endBoundEntityFace" : qUnion([Q1]), "offsetDistance" : 25 * mm});
        }
        {
            var Q0;
            Q0=makeQuery(id+"F13.opBoolean","MERGE",FACE,{"derivedFrom":[makeQuery(id+"F10.opExtrude","SWEPT_FACE",FACE,{"disambiguationData":[OSD([sQuery(id+"F9.wireOp",EDGE,"E81.0")])]}),makeQuery(id+"F10.opExtrude","SWEPT_FACE",FACE,{"disambiguationData":[OSD([sQuery(id+"F9.wireOp",EDGE,"E85.0")])]}),makeQuery(id+"F10.opExtrude","SWEPT_FACE",FACE,{"disambiguationData":[OSD([sQuery(id+"F9.wireOp",EDGE,"E89.0")])]}),makeQuery(id+"F10.opExtrude","SWEPT_FACE",FACE,{"disambiguationData":[OSD([sQuery(id+"F9.wireOp",EDGE,"E93.0")])]}),makeQuery(id+"F10.opExtrude","SWEPT_FACE",FACE,{"disambiguationData":[OSD([sQuery(id+"F9.wireOp",EDGE,"E97.0")])]}),makeQuery(id+"F10.opExtrude","SWEPT_FACE",FACE,{"disambiguationData":[OSD([sQuery(id+"F9.wireOp",EDGE,"E101.0")])]}),makeQuery(id+"F12.opExtrude","SWEPT_FACE",FACE,{"disambiguationData":[OSD([sQuery(id+"F11.wireOp",EDGE,"E105.left")])]})]});
            var sketch = newSketch(context, id + "F26", { "sketchPlane" : qUnion([Q0])});
            skLineSegment(sketch, "E162.bottom", {"start": v(-103, -91.56) * mm, "end": v(-99, -91.56) * mm});
            skLineSegment(sketch, "E162.top", {"start": v(-103, -74.22) * mm, "end": v(-99, -74.22) * mm});
            skLineSegment(sketch, "E162.left", {"start": v(-103, -91.56) * mm, "end": v(-103, -74.22) * mm});
            skLineSegment(sketch, "E162.right", {"start": v(-99, -91.56) * mm, "end": v(-99, -74.22) * mm});
            skLineSegment(sketch, "E163.1.0.0", {"start": v(-99, -59.66) * mm, "end": v(-99, -42.32) * mm});
            skLineSegment(sketch, "E163.1.0.1", {"start": v(-103, -59.66) * mm, "end": v(-99, -59.66) * mm});
            skLineSegment(sketch, "E163.1.0.2", {"start": v(-103, -59.66) * mm, "end": v(-103, -42.32) * mm});
            skLineSegment(sketch, "E163.1.0.3", {"start": v(-103, -42.32) * mm, "end": v(-99, -42.32) * mm});
            skLineSegment(sketch, "E163.2.0.0", {"start": v(-98.98, -27.76) * mm, "end": v(-98.98, -10.42) * mm});
            skLineSegment(sketch, "E163.2.0.1", {"start": v(-102.98, -27.76) * mm, "end": v(-98.98, -27.76) * mm});
            skLineSegment(sketch, "E163.2.0.2", {"start": v(-102.98, -27.76) * mm, "end": v(-102.98, -10.42) * mm});
            skLineSegment(sketch, "E163.2.0.3", {"start": v(-102.98, -10.42) * mm, "end": v(-98.98, -10.42) * mm});
            skLineSegment(sketch, "E163.3.0.0", {"start": v(-98.97, 4.14) * mm, "end": v(-98.97, 21.48) * mm});
            skLineSegment(sketch, "E163.3.0.1", {"start": v(-102.97, 4.14) * mm, "end": v(-98.97, 4.14) * mm});
            skLineSegment(sketch, "E163.3.0.2", {"start": v(-102.97, 4.14) * mm, "end": v(-102.97, 21.48) * mm});
            skLineSegment(sketch, "E163.3.0.3", {"start": v(-102.97, 21.48) * mm, "end": v(-98.97, 21.48) * mm});
            skLineSegment(sketch, "E163.4.0.0", {"start": v(-98.97, 36.04) * mm, "end": v(-98.97, 53.38) * mm});
            skLineSegment(sketch, "E163.4.0.1", {"start": v(-102.97, 36.04) * mm, "end": v(-98.97, 36.04) * mm});
            skLineSegment(sketch, "E163.4.0.2", {"start": v(-102.97, 36.04) * mm, "end": v(-102.97, 53.38) * mm});
            skLineSegment(sketch, "E163.4.0.3", {"start": v(-102.97, 53.38) * mm, "end": v(-98.97, 53.38) * mm});
            skLineSegment(sketch, "E163.5.0.0", {"start": v(-98.96, 67.94) * mm, "end": v(-98.96, 85.28) * mm});
            skLineSegment(sketch, "E163.5.0.1", {"start": v(-102.96, 67.94) * mm, "end": v(-98.96, 67.94) * mm});
            skLineSegment(sketch, "E163.5.0.2", {"start": v(-102.96, 67.94) * mm, "end": v(-102.96, 85.28) * mm});
            skLineSegment(sketch, "E163.5.0.3", {"start": v(-102.96, 85.28) * mm, "end": v(-98.96, 85.28) * mm});
            skLineSegment(sketch, "E163.direction1", {"start": v(-99, -91.56) * mm, "end": v(-99, -59.66) * mm, "construction": true});
            skSolve(sketch);
        }
        {
            var Q0;
            Q0 = qSketchRegion(id + "F26", true);
            var Q1;
            Q1=makeQuery(id+"F13.opBoolean","MERGE",FACE,{"derivedFrom":[makeQuery(id+"F10.opExtrude","SWEPT_FACE",FACE,{"disambiguationData":[OSD([sQuery(id+"F9.wireOp",EDGE,"E83.0")])]}),makeQuery(id+"F10.opExtrude","SWEPT_FACE",FACE,{"disambiguationData":[OSD([sQuery(id+"F9.wireOp",EDGE,"E87.0")])]}),makeQuery(id+"F10.opExtrude","SWEPT_FACE",FACE,{"disambiguationData":[OSD([sQuery(id+"F9.wireOp",EDGE,"E91.0")])]}),makeQuery(id+"F10.opExtrude","SWEPT_FACE",FACE,{"disambiguationData":[OSD([sQuery(id+"F9.wireOp",EDGE,"E95.0")])]}),makeQuery(id+"F10.opExtrude","SWEPT_FACE",FACE,{"disambiguationData":[OSD([sQuery(id+"F9.wireOp",EDGE,"E99.0")])]}),makeQuery(id+"F10.opExtrude","SWEPT_FACE",FACE,{"disambiguationData":[OSD([sQuery(id+"F9.wireOp",EDGE,"E103.0")])]}),makeQuery(id+"F12.opExtrude","SWEPT_FACE",FACE,{"disambiguationData":[OSD([sQuery(id+"F11.wireOp",EDGE,"E105.right")])]})]});
            extrude(context, id + "F27", {"entities" : qUnion([Q0]), "operationType" : NewBodyOperationType.REMOVE, "endBound" : BoundingType.UP_TO_SURFACE, "oppositeDirection" : true, "depth" : 25 * mm, "endBoundEntityFace" : qUnion([Q1]), "offsetDistance" : 25 * mm});
        }
        {
            var Q0;
            Q0=makeQuery(id+"F27.boolean.opBoolean","COPY",FACE,{"derivedFrom":makeQuery(id+"F27.opExtrude","SWEPT_FACE",FACE,{"disambiguationData":[OSD([sQuery(id+"F26.wireOp",EDGE,"E163.1.0.2")])]})});
            var Q1;
            Q1=makeQuery(id+"F27.boolean.opBoolean","COPY",FACE,{"derivedFrom":makeQuery(id+"F27.opExtrude","SWEPT_FACE",FACE,{"disambiguationData":[OSD([sQuery(id+"F26.wireOp",EDGE,"E163.2.0.2")])]})});
            var Q2;
            Q2=makeQuery(id+"F27.boolean.opBoolean","COPY",FACE,{"derivedFrom":makeQuery(id+"F27.opExtrude","SWEPT_FACE",FACE,{"disambiguationData":[OSD([sQuery(id+"F26.wireOp",EDGE,"E163.3.0.2")])]})});
            var Q3;
            Q3=makeQuery(id+"F27.boolean.opBoolean","COPY",FACE,{"derivedFrom":makeQuery(id+"F27.opExtrude","SWEPT_FACE",FACE,{"disambiguationData":[OSD([sQuery(id+"F26.wireOp",EDGE,"E163.4.0.2")])]})});
            var Q4;
            Q4=makeQuery(id+"F27.boolean.opBoolean","COPY",FACE,{"derivedFrom":makeQuery(id+"F27.opExtrude","SWEPT_FACE",FACE,{"disambiguationData":[OSD([sQuery(id+"F26.wireOp",EDGE,"E163.5.0.2")])]})});
            extrude(context, id + "F28", {"entities" : qUnion([Q0, Q1, Q2, Q3, Q4]), "operationType" : NewBodyOperationType.REMOVE, "oppositeDirection" : true, "depth" : 25 * mm, "offsetDistance" : 25 * mm});
        }
        {
            var Q0;
            Q0=makeQuery(id+"F8.opBoolean","MERGE",FACE,{"derivedFrom":[makeQuery(id+"F5.opExtrude","SWEPT_FACE",FACE,{"disambiguationData":[OSD([sQuery(id+"F4.wireOp",EDGE,"E56.0")])]}),makeQuery(id+"F5.opExtrude","SWEPT_FACE",FACE,{"disambiguationData":[OSD([sQuery(id+"F4.wireOp",EDGE,"E60.0")])]}),makeQuery(id+"F5.opExtrude","SWEPT_FACE",FACE,{"disambiguationData":[OSD([sQuery(id+"F4.wireOp",EDGE,"E64.0")])]}),makeQuery(id+"F5.opExtrude","SWEPT_FACE",FACE,{"disambiguationData":[OSD([sQuery(id+"F4.wireOp",EDGE,"E68.0")])]}),makeQuery(id+"F5.opExtrude","SWEPT_FACE",FACE,{"disambiguationData":[OSD([sQuery(id+"F4.wireOp",EDGE,"E72.0")])]}),makeQuery(id+"F5.opExtrude","SWEPT_FACE",FACE,{"disambiguationData":[OSD([sQuery(id+"F4.wireOp",EDGE,"E76.0")])]}),makeQuery(id+"F7.opExtrude","SWEPT_FACE",FACE,{"disambiguationData":[OSD([sQuery(id+"F6.wireOp",EDGE,"E80.bottom")])]})]});
            var sketch = newSketch(context, id + "F29", { "sketchPlane" : qUnion([Q0])});
            skLineSegment(sketch, "E164.bottom", {"start": v(89.2, -103) * mm, "end": v(71.86, -103) * mm});
            skLineSegment(sketch, "E164.top", {"start": v(89.2, -99) * mm, "end": v(71.86, -99) * mm});
            skLineSegment(sketch, "E164.left", {"start": v(89.2, -103) * mm, "end": v(89.2, -99) * mm});
            skLineSegment(sketch, "E164.right", {"start": v(71.86, -103) * mm, "end": v(71.86, -99) * mm});
            skLineSegment(sketch, "E165.1.0.0", {"start": v(57.2, -103) * mm, "end": v(57.2, -99) * mm});
            skLineSegment(sketch, "E165.1.0.1", {"start": v(57.2, -99) * mm, "end": v(39.86, -99) * mm});
            skLineSegment(sketch, "E165.1.0.2", {"start": v(39.86, -103) * mm, "end": v(39.86, -99) * mm});
            skLineSegment(sketch, "E165.1.0.3", {"start": v(57.2, -103) * mm, "end": v(39.86, -103) * mm});
            skLineSegment(sketch, "E165.2.0.0", {"start": v(25.2, -103) * mm, "end": v(25.2, -99) * mm});
            skLineSegment(sketch, "E165.2.0.1", {"start": v(25.2, -99) * mm, "end": v(7.86, -99) * mm});
            skLineSegment(sketch, "E165.2.0.2", {"start": v(7.86, -103) * mm, "end": v(7.86, -99) * mm});
            skLineSegment(sketch, "E165.2.0.3", {"start": v(25.2, -103) * mm, "end": v(7.86, -103) * mm});
            skLineSegment(sketch, "E165.3.0.0", {"start": v(-6.8, -103) * mm, "end": v(-6.8, -99) * mm});
            skLineSegment(sketch, "E165.3.0.1", {"start": v(-6.8, -99) * mm, "end": v(-24.14, -99) * mm});
            skLineSegment(sketch, "E165.3.0.2", {"start": v(-24.14, -103) * mm, "end": v(-24.14, -99) * mm});
            skLineSegment(sketch, "E165.3.0.3", {"start": v(-6.8, -103) * mm, "end": v(-24.14, -103) * mm});
            skLineSegment(sketch, "E165.4.0.0", {"start": v(-38.8, -103) * mm, "end": v(-38.8, -99) * mm});
            skLineSegment(sketch, "E165.4.0.1", {"start": v(-38.8, -99) * mm, "end": v(-56.14, -99) * mm});
            skLineSegment(sketch, "E165.4.0.2", {"start": v(-56.14, -103) * mm, "end": v(-56.14, -99) * mm});
            skLineSegment(sketch, "E165.4.0.3", {"start": v(-38.8, -103) * mm, "end": v(-56.14, -103) * mm});
            skLineSegment(sketch, "E165.5.0.0", {"start": v(-70.8, -103) * mm, "end": v(-70.8, -99) * mm});
            skLineSegment(sketch, "E165.5.0.1", {"start": v(-70.8, -99) * mm, "end": v(-88.14, -99) * mm});
            skLineSegment(sketch, "E165.5.0.2", {"start": v(-88.14, -103) * mm, "end": v(-88.14, -99) * mm});
            skLineSegment(sketch, "E165.5.0.3", {"start": v(-70.8, -103) * mm, "end": v(-88.14, -103) * mm});
            skLineSegment(sketch, "E165.direction1", {"start": v(89.2, -103) * mm, "end": v(57.2, -103) * mm, "construction": true});
            skSolve(sketch);
        }
        {
            var Q0;
            Q0 = qSketchRegion(id + "F29", true);
            var Q1;
            Q1=makeQuery(id+"F8.opBoolean","MERGE",FACE,{"derivedFrom":[makeQuery(id+"F5.opExtrude","SWEPT_FACE",FACE,{"disambiguationData":[OSD([sQuery(id+"F4.wireOp",EDGE,"E58.0")])]}),makeQuery(id+"F5.opExtrude","SWEPT_FACE",FACE,{"disambiguationData":[OSD([sQuery(id+"F4.wireOp",EDGE,"E62.0")])]}),makeQuery(id+"F5.opExtrude","SWEPT_FACE",FACE,{"disambiguationData":[OSD([sQuery(id+"F4.wireOp",EDGE,"E66.0")])]}),makeQuery(id+"F5.opExtrude","SWEPT_FACE",FACE,{"disambiguationData":[OSD([sQuery(id+"F4.wireOp",EDGE,"E70.0")])]}),makeQuery(id+"F5.opExtrude","SWEPT_FACE",FACE,{"disambiguationData":[OSD([sQuery(id+"F4.wireOp",EDGE,"E74.0")])]}),makeQuery(id+"F5.opExtrude","SWEPT_FACE",FACE,{"disambiguationData":[OSD([sQuery(id+"F4.wireOp",EDGE,"E78.0")])]}),makeQuery(id+"F7.opExtrude","SWEPT_FACE",FACE,{"disambiguationData":[OSD([sQuery(id+"F6.wireOp",EDGE,"E80.top")])]})]});
            extrude(context, id + "F30", {"entities" : qUnion([Q0]), "operationType" : NewBodyOperationType.REMOVE, "endBound" : BoundingType.UP_TO_SURFACE, "oppositeDirection" : true, "depth" : 25 * mm, "endBoundEntityFace" : qUnion([Q1]), "offsetDistance" : 25 * mm});
        }
        {
            var Q0;
            Q0=makeQuery(id+"F23.opBoolean","MERGE",FACE,{"derivedFrom":[makeQuery(id+"F20.opExtrude","SWEPT_FACE",FACE,{"disambiguationData":[OSD([sQuery(id+"F19.wireOp",EDGE,"E132.0")])]}),makeQuery(id+"F20.opExtrude","SWEPT_FACE",FACE,{"disambiguationData":[OSD([sQuery(id+"F19.wireOp",EDGE,"E135.0")])]}),makeQuery(id+"F20.opExtrude","SWEPT_FACE",FACE,{"disambiguationData":[OSD([sQuery(id+"F19.wireOp",EDGE,"E139.0")])]}),makeQuery(id+"F20.opExtrude","SWEPT_FACE",FACE,{"disambiguationData":[OSD([sQuery(id+"F19.wireOp",EDGE,"E143.0")])]}),makeQuery(id+"F20.opExtrude","SWEPT_FACE",FACE,{"disambiguationData":[OSD([sQuery(id+"F19.wireOp",EDGE,"E147.0")])]}),makeQuery(id+"F20.opExtrude","SWEPT_FACE",FACE,{"disambiguationData":[OSD([sQuery(id+"F19.wireOp",EDGE,"E151.0")])]}),makeQuery(id+"F22.opExtrude","SWEPT_FACE",FACE,{"disambiguationData":[OSD([sQuery(id+"F21.wireOp",EDGE,"E155.left")])]})]});
            var sketch = newSketch(context, id + "F31", { "sketchPlane" : qUnion([Q0])});
            skLineSegment(sketch, "E166.bottom", {"start": v(103, 88.42) * mm, "end": v(99, 88.42) * mm});
            skLineSegment(sketch, "E166.top", {"start": v(103, 71.08) * mm, "end": v(99, 71.08) * mm});
            skLineSegment(sketch, "E166.left", {"start": v(103, 88.42) * mm, "end": v(103, 71.08) * mm});
            skLineSegment(sketch, "E166.right", {"start": v(99, 88.42) * mm, "end": v(99, 71.08) * mm});
            skLineSegment(sketch, "E167.1.0.0", {"start": v(99, 56.52) * mm, "end": v(99, 39.18) * mm});
            skLineSegment(sketch, "E167.1.0.1", {"start": v(103, 56.52) * mm, "end": v(99, 56.52) * mm});
            skLineSegment(sketch, "E167.1.0.2", {"start": v(103, 56.52) * mm, "end": v(103, 39.18) * mm});
            skLineSegment(sketch, "E167.1.0.3", {"start": v(103, 39.18) * mm, "end": v(99, 39.18) * mm});
            skLineSegment(sketch, "E167.2.0.0", {"start": v(99, 24.62) * mm, "end": v(99, 7.28) * mm});
            skLineSegment(sketch, "E167.2.0.1", {"start": v(103, 24.62) * mm, "end": v(99, 24.62) * mm});
            skLineSegment(sketch, "E167.2.0.2", {"start": v(103, 24.62) * mm, "end": v(103, 7.28) * mm});
            skLineSegment(sketch, "E167.2.0.3", {"start": v(103, 7.28) * mm, "end": v(99, 7.28) * mm});
            skLineSegment(sketch, "E167.3.0.0", {"start": v(99, -7.28) * mm, "end": v(99, -24.62) * mm});
            skLineSegment(sketch, "E167.3.0.1", {"start": v(103, -7.28) * mm, "end": v(99, -7.28) * mm});
            skLineSegment(sketch, "E167.3.0.2", {"start": v(103, -7.28) * mm, "end": v(103, -24.62) * mm});
            skLineSegment(sketch, "E167.3.0.3", {"start": v(103, -24.62) * mm, "end": v(99, -24.62) * mm});
            skLineSegment(sketch, "E167.4.0.0", {"start": v(99, -39.18) * mm, "end": v(99, -56.52) * mm});
            skLineSegment(sketch, "E167.4.0.1", {"start": v(103, -39.18) * mm, "end": v(99, -39.18) * mm});
            skLineSegment(sketch, "E167.4.0.2", {"start": v(103, -39.18) * mm, "end": v(103, -56.52) * mm});
            skLineSegment(sketch, "E167.4.0.3", {"start": v(103, -56.52) * mm, "end": v(99, -56.52) * mm});
            skLineSegment(sketch, "E167.5.0.0", {"start": v(99, -71.08) * mm, "end": v(99, -88.42) * mm});
            skLineSegment(sketch, "E167.5.0.1", {"start": v(103, -71.08) * mm, "end": v(99, -71.08) * mm});
            skLineSegment(sketch, "E167.5.0.2", {"start": v(103, -71.08) * mm, "end": v(103, -88.42) * mm});
            skLineSegment(sketch, "E167.5.0.3", {"start": v(103, -88.42) * mm, "end": v(99, -88.42) * mm});
            skLineSegment(sketch, "E167.direction1", {"start": v(99, 71.08) * mm, "end": v(99, 39.18) * mm, "construction": true});
            skSolve(sketch);
        }
        {
            var Q0;
            Q0 = qSketchRegion(id + "F31", true);
            var Q1;
            Q1=makeQuery(id+"F23.opBoolean","MERGE",FACE,{"derivedFrom":[makeQuery(id+"F20.opExtrude","SWEPT_FACE",FACE,{"disambiguationData":[OSD([sQuery(id+"F19.wireOp",EDGE,"E133.0")])]}),makeQuery(id+"F20.opExtrude","SWEPT_FACE",FACE,{"disambiguationData":[OSD([sQuery(id+"F19.wireOp",EDGE,"E137.0")])]}),makeQuery(id+"F20.opExtrude","SWEPT_FACE",FACE,{"disambiguationData":[OSD([sQuery(id+"F19.wireOp",EDGE,"E141.0")])]}),makeQuery(id+"F20.opExtrude","SWEPT_FACE",FACE,{"disambiguationData":[OSD([sQuery(id+"F19.wireOp",EDGE,"E145.0")])]}),makeQuery(id+"F20.opExtrude","SWEPT_FACE",FACE,{"disambiguationData":[OSD([sQuery(id+"F19.wireOp",EDGE,"E149.0")])]}),makeQuery(id+"F20.opExtrude","SWEPT_FACE",FACE,{"disambiguationData":[OSD([sQuery(id+"F19.wireOp",EDGE,"E153.0")])]}),makeQuery(id+"F22.opExtrude","SWEPT_FACE",FACE,{"disambiguationData":[OSD([sQuery(id+"F21.wireOp",EDGE,"E155.right")])]})]});
            extrude(context, id + "F32", {"entities" : qUnion([Q0]), "operationType" : NewBodyOperationType.REMOVE, "endBound" : BoundingType.UP_TO_SURFACE, "oppositeDirection" : true, "depth" : 25 * mm, "endBoundEntityFace" : qUnion([Q1]), "offsetDistance" : 25 * mm});
        }
        {
            var Q0;
            Q0=makeQuery(id+"F18.opBoolean","MERGE",FACE,{"derivedFrom":[makeQuery(id+"F15.opExtrude","SWEPT_FACE",FACE,{"disambiguationData":[OSD([sQuery(id+"F14.wireOp",EDGE,"E106.0")])]}),makeQuery(id+"F15.opExtrude","SWEPT_FACE",FACE,{"disambiguationData":[OSD([sQuery(id+"F14.wireOp",EDGE,"E110.0")])]}),makeQuery(id+"F15.opExtrude","SWEPT_FACE",FACE,{"disambiguationData":[OSD([sQuery(id+"F14.wireOp",EDGE,"E114.0")])]}),makeQuery(id+"F15.opExtrude","SWEPT_FACE",FACE,{"disambiguationData":[OSD([sQuery(id+"F14.wireOp",EDGE,"E118.0")])]}),makeQuery(id+"F15.opExtrude","SWEPT_FACE",FACE,{"disambiguationData":[OSD([sQuery(id+"F14.wireOp",EDGE,"E122.0")])]}),makeQuery(id+"F15.opExtrude","SWEPT_FACE",FACE,{"disambiguationData":[OSD([sQuery(id+"F14.wireOp",EDGE,"E126.0")])]}),makeQuery(id+"F17.opExtrude","SWEPT_FACE",FACE,{"disambiguationData":[OSD([sQuery(id+"F16.wireOp",EDGE,"E130.bottom")])]})]});
            var sketch = newSketch(context, id + "F33", { "sketchPlane" : qUnion([Q0])});
            skLineSegment(sketch, "E168.bottom", {"start": v(-90.54, 103) * mm, "end": v(-73.2, 103) * mm});
            skLineSegment(sketch, "E168.top", {"start": v(-90.54, 99) * mm, "end": v(-73.2, 99) * mm});
            skLineSegment(sketch, "E168.left", {"start": v(-90.54, 103) * mm, "end": v(-90.54, 99) * mm});
            skLineSegment(sketch, "E168.right", {"start": v(-73.2, 103) * mm, "end": v(-73.2, 99) * mm});
            skLineSegment(sketch, "E169.1.0.0", {"start": v(-58.54, 99) * mm, "end": v(-41.2, 99) * mm});
            skLineSegment(sketch, "E169.1.0.1", {"start": v(-58.54, 103) * mm, "end": v(-58.54, 99) * mm});
            skLineSegment(sketch, "E169.1.0.2", {"start": v(-58.54, 103) * mm, "end": v(-41.2, 103) * mm});
            skLineSegment(sketch, "E169.1.0.3", {"start": v(-41.2, 103) * mm, "end": v(-41.2, 99) * mm});
            skLineSegment(sketch, "E169.2.0.0", {"start": v(-26.54, 99) * mm, "end": v(-9.2, 99) * mm});
            skLineSegment(sketch, "E169.2.0.1", {"start": v(-26.54, 103) * mm, "end": v(-26.54, 99) * mm});
            skLineSegment(sketch, "E169.2.0.2", {"start": v(-26.54, 103) * mm, "end": v(-9.2, 103) * mm});
            skLineSegment(sketch, "E169.2.0.3", {"start": v(-9.2, 103) * mm, "end": v(-9.2, 99) * mm});
            skLineSegment(sketch, "E169.3.0.0", {"start": v(5.46, 99) * mm, "end": v(22.8, 99) * mm});
            skLineSegment(sketch, "E169.3.0.1", {"start": v(5.46, 103) * mm, "end": v(5.46, 99) * mm});
            skLineSegment(sketch, "E169.3.0.2", {"start": v(5.46, 103) * mm, "end": v(22.8, 103) * mm});
            skLineSegment(sketch, "E169.3.0.3", {"start": v(22.8, 103) * mm, "end": v(22.8, 99) * mm});
            skLineSegment(sketch, "E169.4.0.0", {"start": v(37.46, 99) * mm, "end": v(54.8, 99) * mm});
            skLineSegment(sketch, "E169.4.0.1", {"start": v(37.46, 103) * mm, "end": v(37.46, 99) * mm});
            skLineSegment(sketch, "E169.4.0.2", {"start": v(37.46, 103) * mm, "end": v(54.8, 103) * mm});
            skLineSegment(sketch, "E169.4.0.3", {"start": v(54.8, 103) * mm, "end": v(54.8, 99) * mm});
            skLineSegment(sketch, "E169.5.0.0", {"start": v(69.46, 99) * mm, "end": v(86.8, 99) * mm});
            skLineSegment(sketch, "E169.5.0.1", {"start": v(69.46, 103) * mm, "end": v(69.46, 99) * mm});
            skLineSegment(sketch, "E169.5.0.2", {"start": v(69.46, 103) * mm, "end": v(86.8, 103) * mm});
            skLineSegment(sketch, "E169.5.0.3", {"start": v(86.8, 103) * mm, "end": v(86.8, 99) * mm});
            skLineSegment(sketch, "E169.direction1", {"start": v(-90.54, 99) * mm, "end": v(-58.54, 99) * mm, "construction": true});
            skSolve(sketch);
        }
        {
            var Q0;
            Q0 = qSketchRegion(id + "F33", true);
            var Q1;
            Q1=makeQuery(id+"F18.opBoolean","MERGE",FACE,{"derivedFrom":[makeQuery(id+"F15.opExtrude","SWEPT_FACE",FACE,{"disambiguationData":[OSD([sQuery(id+"F14.wireOp",EDGE,"E108.0")])]}),makeQuery(id+"F15.opExtrude","SWEPT_FACE",FACE,{"disambiguationData":[OSD([sQuery(id+"F14.wireOp",EDGE,"E112.0")])]}),makeQuery(id+"F15.opExtrude","SWEPT_FACE",FACE,{"disambiguationData":[OSD([sQuery(id+"F14.wireOp",EDGE,"E116.0")])]}),makeQuery(id+"F15.opExtrude","SWEPT_FACE",FACE,{"disambiguationData":[OSD([sQuery(id+"F14.wireOp",EDGE,"E120.0")])]}),makeQuery(id+"F15.opExtrude","SWEPT_FACE",FACE,{"disambiguationData":[OSD([sQuery(id+"F14.wireOp",EDGE,"E124.0")])]}),makeQuery(id+"F15.opExtrude","SWEPT_FACE",FACE,{"disambiguationData":[OSD([sQuery(id+"F14.wireOp",EDGE,"E128.0")])]}),makeQuery(id+"F17.opExtrude","SWEPT_FACE",FACE,{"disambiguationData":[OSD([sQuery(id+"F16.wireOp",EDGE,"E130.top")])]})]});
            extrude(context, id + "F34", {"entities" : qUnion([Q0]), "operationType" : NewBodyOperationType.REMOVE, "endBound" : BoundingType.UP_TO_SURFACE, "oppositeDirection" : true, "depth" : 25 * mm, "endBoundEntityFace" : qUnion([Q1]), "offsetDistance" : 25 * mm});
        }
        {
            var Q0;
            Q0=makeQuery(id+"F30.boolean.opBoolean","COPY",FACE,{"derivedFrom":makeQuery(id+"F30.opExtrude","SWEPT_FACE",FACE,{"disambiguationData":[OSD([sQuery(id+"F29.wireOp",EDGE,"E165.2.0.1")])]})});
            var sketch = newSketch(context, id + "F35", { "sketchPlane" : qUnion([Q0])});
            skLineSegment(sketch, "E170.0", {"start": v(-100, 100) * mm, "end": v(100, 100) * mm});
            skLineSegment(sketch, "E170.1", {"start": v(-100, 100) * mm, "end": v(-100, -100) * mm});
            skLineSegment(sketch, "E170.2", {"start": v(-100, -100) * mm, "end": v(100, -100) * mm});
            skLineSegment(sketch, "E170.3", {"start": v(100, 100) * mm, "end": v(100, -100) * mm});
            skLineSegment(sketch, "E171.0", {"start": v(-70.8, 95.6) * mm, "end": v(-56.14, 95.6) * mm});
            skLineSegment(sketch, "E171.1", {"start": v(-56.14, 91.6) * mm, "end": v(-56.14, 95.6) * mm});
            skLineSegment(sketch, "E171.2", {"start": v(-70.8, 91.6) * mm, "end": v(-56.14, 91.6) * mm});
            skLineSegment(sketch, "E171.3", {"start": v(-70.8, 91.6) * mm, "end": v(-70.8, 95.6) * mm});
            skLineSegment(sketch, "E172.0", {"start": v(-38.8, 95.6) * mm, "end": v(-24.14, 95.6) * mm});
            skLineSegment(sketch, "E173.0", {"start": v(-38.8, 91.6) * mm, "end": v(-38.8, 95.6) * mm});
            skLineSegment(sketch, "E174.0", {"start": v(-38.8, 91.6) * mm, "end": v(-24.14, 91.6) * mm});
            skLineSegment(sketch, "E175.0", {"start": v(-24.14, 91.6) * mm, "end": v(-24.14, 95.6) * mm});
            skLineSegment(sketch, "E176.0", {"start": v(-6.8, 95.6) * mm, "end": v(7.86, 95.6) * mm});
            skLineSegment(sketch, "E177.0", {"start": v(-6.8, 91.6) * mm, "end": v(-6.8, 95.6) * mm});
            skLineSegment(sketch, "E178.0", {"start": v(-6.8, 91.6) * mm, "end": v(7.86, 91.6) * mm});
            skLineSegment(sketch, "E179.0", {"start": v(7.86, 91.6) * mm, "end": v(7.86, 95.6) * mm});
            skLineSegment(sketch, "E180.0", {"start": v(25.2, 95.6) * mm, "end": v(39.86, 95.6) * mm});
            skLineSegment(sketch, "E181.0", {"start": v(25.2, 91.6) * mm, "end": v(25.2, 95.6) * mm});
            skLineSegment(sketch, "E182.0", {"start": v(25.2, 91.6) * mm, "end": v(39.86, 91.6) * mm});
            skLineSegment(sketch, "E183.0", {"start": v(39.86, 91.6) * mm, "end": v(39.86, 95.6) * mm});
            skLineSegment(sketch, "E184.0", {"start": v(57.2, 95.6) * mm, "end": v(71.86, 95.6) * mm});
            skLineSegment(sketch, "E185.0", {"start": v(57.2, 91.6) * mm, "end": v(57.2, 95.6) * mm});
            skLineSegment(sketch, "E186.0", {"start": v(57.2, 91.6) * mm, "end": v(71.86, 91.6) * mm});
            skLineSegment(sketch, "E187.0", {"start": v(71.86, 91.6) * mm, "end": v(71.86, 95.6) * mm});
            skLineSegment(sketch, "E188.0", {"start": v(89.2, 91.6) * mm, "end": v(89.2, 95.6) * mm});
            skLineSegment(sketch, "E189.0", {"start": v(89.2, 95.6) * mm, "end": v(95.6, 95.6) * mm});
            skLineSegment(sketch, "E190.0", {"start": v(89.2, 91.6) * mm, "end": v(95.6, 91.6) * mm});
            skLineSegment(sketch, "E191.0", {"start": v(95.6, 95.6) * mm, "end": v(95.6, 91.6) * mm});
            skLineSegment(sketch, "E192.0", {"start": v(91.6, 91.72) * mm, "end": v(91.6, 85.28) * mm});
            skLineSegment(sketch, "E193.0", {"start": v(95.6, 91.72) * mm, "end": v(95.6, 85.28) * mm});
            skLineSegment(sketch, "E194.0", {"start": v(95.6, 85.28) * mm, "end": v(91.6, 85.28) * mm});
            skLineSegment(sketch, "E195.0", {"start": v(95.6, 67.94) * mm, "end": v(91.6, 67.94) * mm});
            skPoint(sketch, "E196.0", {"position": v(91.6, 60.66) * mm});
            skLineSegment(sketch, "E197.0", {"start": v(95.6, 67.94) * mm, "end": v(95.6, 53.38) * mm});
            skLineSegment(sketch, "E198.0", {"start": v(95.6, 53.38) * mm, "end": v(91.6, 53.38) * mm});
            skLineSegment(sketch, "E199.0", {"start": v(91.6, 67.94) * mm, "end": v(91.6, 53.38) * mm});
            skLineSegment(sketch, "E200.0", {"start": v(91.6, 36.04) * mm, "end": v(91.6, 21.48) * mm});
            skLineSegment(sketch, "E201.0", {"start": v(95.6, 36.04) * mm, "end": v(95.6, 21.48) * mm});
            skLineSegment(sketch, "E202.0", {"start": v(95.6, 21.48) * mm, "end": v(91.6, 21.48) * mm});
            skLineSegment(sketch, "E203.0", {"start": v(95.6, 36.04) * mm, "end": v(91.6, 36.04) * mm});
            skLineSegment(sketch, "E204.0", {"start": v(95.6, 4.14) * mm, "end": v(91.6, 4.14) * mm});
            skLineSegment(sketch, "E205.0", {"start": v(95.6, 4.14) * mm, "end": v(95.6, -10.42) * mm});
            skLineSegment(sketch, "E206.0", {"start": v(91.6, 4.14) * mm, "end": v(91.6, -10.42) * mm});
            skLineSegment(sketch, "E207.0", {"start": v(95.6, -10.42) * mm, "end": v(91.6, -10.42) * mm});
            skLineSegment(sketch, "E208.0", {"start": v(95.6, -27.76) * mm, "end": v(91.6, -27.76) * mm});
            skLineSegment(sketch, "E209.0", {"start": v(91.6, -27.76) * mm, "end": v(91.6, -42.32) * mm});
            skLineSegment(sketch, "E210.0", {"start": v(95.6, -27.76) * mm, "end": v(95.6, -42.32) * mm});
            skLineSegment(sketch, "E211.0", {"start": v(95.6, -42.32) * mm, "end": v(91.6, -42.32) * mm});
            skLineSegment(sketch, "E212.0", {"start": v(91.6, -59.66) * mm, "end": v(91.6, -74.22) * mm});
            skLineSegment(sketch, "E213.0", {"start": v(95.6, -59.66) * mm, "end": v(95.6, -74.22) * mm});
            skLineSegment(sketch, "E214.0", {"start": v(91.6, -74.22) * mm, "end": v(95.6, -74.22) * mm});
            skLineSegment(sketch, "E215.0", {"start": v(91.6, -91.56) * mm, "end": v(95.6, -91.56) * mm});
            skLineSegment(sketch, "E216.0", {"start": v(95.6, -91.56) * mm, "end": v(95.6, -95.56) * mm});
            skLineSegment(sketch, "E217.0", {"start": v(95.6, -95.56) * mm, "end": v(91.6, -95.56) * mm});
            skLineSegment(sketch, "E218.0", {"start": v(91.6, -91.56) * mm, "end": v(91.6, -95.56) * mm});
            skLineSegment(sketch, "E219.0.0", {"start": v(91.53, -91.6) * mm, "end": v(86.8, -91.6) * mm});
            skLineSegment(sketch, "E219.0.1", {"start": v(86.8, -91.6) * mm, "end": v(86.8, -95.6) * mm});
            skLineSegment(sketch, "E219.0.2", {"start": v(86.8, -95.6) * mm, "end": v(91.53, -95.6) * mm});
            skLineSegment(sketch, "E219.0.3", {"start": v(91.53, -95.6) * mm, "end": v(91.53, -91.6) * mm});
            skLineSegment(sketch, "E220.0.0", {"start": v(69.46, -91.6) * mm, "end": v(54.8, -91.6) * mm});
            skLineSegment(sketch, "E220.0.1", {"start": v(54.8, -91.6) * mm, "end": v(54.8, -95.6) * mm});
            skLineSegment(sketch, "E220.0.2", {"start": v(54.8, -95.6) * mm, "end": v(69.46, -95.6) * mm});
            skLineSegment(sketch, "E220.0.3", {"start": v(69.46, -95.6) * mm, "end": v(69.46, -91.6) * mm});
            skLineSegment(sketch, "E221.0.0", {"start": v(37.46, -91.6) * mm, "end": v(22.8, -91.6) * mm});
            skLineSegment(sketch, "E221.0.1", {"start": v(22.8, -91.6) * mm, "end": v(22.8, -95.6) * mm});
            skLineSegment(sketch, "E221.0.2", {"start": v(22.8, -95.6) * mm, "end": v(37.46, -95.6) * mm});
            skLineSegment(sketch, "E221.0.3", {"start": v(37.46, -95.6) * mm, "end": v(37.46, -91.6) * mm});
            skLineSegment(sketch, "E222.0.0", {"start": v(5.46, -91.6) * mm, "end": v(-9.2, -91.6) * mm});
            skLineSegment(sketch, "E222.0.1", {"start": v(-9.2, -91.6) * mm, "end": v(-9.2, -95.6) * mm});
            skLineSegment(sketch, "E222.0.2", {"start": v(-9.2, -95.6) * mm, "end": v(5.46, -95.6) * mm});
            skLineSegment(sketch, "E222.0.3", {"start": v(5.46, -95.6) * mm, "end": v(5.46, -91.6) * mm});
            skLineSegment(sketch, "E223.0.0", {"start": v(-26.54, -91.6) * mm, "end": v(-41.2, -91.6) * mm});
            skLineSegment(sketch, "E223.0.1", {"start": v(-41.2, -91.6) * mm, "end": v(-41.2, -95.6) * mm});
            skLineSegment(sketch, "E223.0.2", {"start": v(-41.2, -95.6) * mm, "end": v(-26.54, -95.6) * mm});
            skLineSegment(sketch, "E223.0.3", {"start": v(-26.54, -95.6) * mm, "end": v(-26.54, -91.6) * mm});
            skLineSegment(sketch, "E224.0.0", {"start": v(-58.54, -91.6) * mm, "end": v(-73.2, -91.6) * mm});
            skLineSegment(sketch, "E224.0.1", {"start": v(-73.2, -91.6) * mm, "end": v(-73.2, -95.6) * mm});
            skLineSegment(sketch, "E224.0.2", {"start": v(-73.2, -95.6) * mm, "end": v(-58.54, -95.6) * mm});
            skLineSegment(sketch, "E224.0.3", {"start": v(-58.54, -95.6) * mm, "end": v(-58.54, -91.6) * mm});
            skLineSegment(sketch, "E225.0.0", {"start": v(-90.54, -95.6) * mm, "end": v(-90.54, -91.6) * mm});
            skLineSegment(sketch, "E225.0.1", {"start": v(-90.54, -91.6) * mm, "end": v(-95.49, -91.6) * mm});
            skLineSegment(sketch, "E225.0.2", {"start": v(-95.49, -91.6) * mm, "end": v(-95.49, -95.6) * mm});
            skLineSegment(sketch, "E225.0.3", {"start": v(-95.49, -95.6) * mm, "end": v(-90.54, -95.6) * mm});
            skLineSegment(sketch, "E226.0.0", {"start": v(-91.6, -91.68) * mm, "end": v(-91.6, -88.42) * mm});
            skLineSegment(sketch, "E226.0.1", {"start": v(-91.6, -88.42) * mm, "end": v(-95.6, -88.42) * mm});
            skLineSegment(sketch, "E226.0.2", {"start": v(-95.6, -88.42) * mm, "end": v(-95.6, -91.68) * mm});
            skLineSegment(sketch, "E226.0.3", {"start": v(-95.6, -91.68) * mm, "end": v(-91.6, -91.68) * mm});
            skLineSegment(sketch, "E227.0.0", {"start": v(-91.6, -71.08) * mm, "end": v(-91.6, -56.52) * mm});
            skLineSegment(sketch, "E227.0.1", {"start": v(-91.6, -56.52) * mm, "end": v(-95.6, -56.52) * mm});
            skLineSegment(sketch, "E227.0.2", {"start": v(-95.6, -56.52) * mm, "end": v(-95.6, -71.08) * mm});
            skLineSegment(sketch, "E227.0.3", {"start": v(-95.6, -71.08) * mm, "end": v(-91.6, -71.08) * mm});
            skLineSegment(sketch, "E228.0.0", {"start": v(-91.6, -39.18) * mm, "end": v(-91.6, -24.62) * mm});
            skLineSegment(sketch, "E228.0.1", {"start": v(-91.6, -24.62) * mm, "end": v(-95.6, -24.62) * mm});
            skLineSegment(sketch, "E228.0.2", {"start": v(-95.6, -24.62) * mm, "end": v(-95.6, -39.18) * mm});
            skLineSegment(sketch, "E228.0.3", {"start": v(-95.6, -39.18) * mm, "end": v(-91.6, -39.18) * mm});
            skLineSegment(sketch, "E229.0.0", {"start": v(-91.6, -7.28) * mm, "end": v(-91.6, 7.28) * mm});
            skLineSegment(sketch, "E229.0.1", {"start": v(-91.6, 7.28) * mm, "end": v(-95.6, 7.28) * mm});
            skLineSegment(sketch, "E229.0.2", {"start": v(-95.6, 7.28) * mm, "end": v(-95.6, -7.28) * mm});
            skLineSegment(sketch, "E229.0.3", {"start": v(-95.6, -7.28) * mm, "end": v(-91.6, -7.28) * mm});
            skLineSegment(sketch, "E230.0.0", {"start": v(-91.6, 24.62) * mm, "end": v(-91.6, 39.18) * mm});
            skLineSegment(sketch, "E230.0.1", {"start": v(-91.6, 39.18) * mm, "end": v(-95.6, 39.18) * mm});
            skLineSegment(sketch, "E230.0.2", {"start": v(-95.6, 39.18) * mm, "end": v(-95.6, 24.62) * mm});
            skLineSegment(sketch, "E230.0.3", {"start": v(-95.6, 24.62) * mm, "end": v(-91.6, 24.62) * mm});
            skLineSegment(sketch, "E231.0.0", {"start": v(-91.6, 56.52) * mm, "end": v(-91.6, 71.08) * mm});
            skLineSegment(sketch, "E231.0.1", {"start": v(-91.6, 71.08) * mm, "end": v(-95.6, 71.08) * mm});
            skLineSegment(sketch, "E231.0.2", {"start": v(-95.6, 71.08) * mm, "end": v(-95.6, 56.52) * mm});
            skLineSegment(sketch, "E231.0.3", {"start": v(-95.6, 56.52) * mm, "end": v(-91.6, 56.52) * mm});
            skLineSegment(sketch, "E232.0.0", {"start": v(-95.6, 88.42) * mm, "end": v(-91.6, 88.42) * mm});
            skLineSegment(sketch, "E232.0.1", {"start": v(-91.6, 88.42) * mm, "end": v(-91.6, 91.74) * mm});
            skLineSegment(sketch, "E232.0.2", {"start": v(-91.6, 91.74) * mm, "end": v(-95.6, 91.74) * mm});
            skLineSegment(sketch, "E232.0.3", {"start": v(-95.6, 91.74) * mm, "end": v(-95.6, 88.42) * mm});
            skLineSegment(sketch, "E233.0.0", {"start": v(-95.6, 91.6) * mm, "end": v(-88.14, 91.6) * mm});
            skLineSegment(sketch, "E233.0.1", {"start": v(-88.14, 91.6) * mm, "end": v(-88.14, 95.6) * mm});
            skLineSegment(sketch, "E233.0.2", {"start": v(-88.14, 95.6) * mm, "end": v(-95.6, 95.6) * mm});
            skLineSegment(sketch, "E233.0.3", {"start": v(-95.6, 95.6) * mm, "end": v(-95.6, 91.6) * mm});
            skLineSegment(sketch, "E234.0.0", {"start": v(95.6, -74.22) * mm, "end": v(95.6, -59.66) * mm});
            skLineSegment(sketch, "E234.0.1", {"start": v(95.6, -59.66) * mm, "end": v(91.6, -59.66) * mm});
            skSolve(sketch);
        }
        {
            var Q0;
            Q0 = qSketchRegion(id + "F35", true);
            extrude(context, id + "F36", {"entities" : qUnion([Q0]), "depth" : 4 * mm, "offsetDistance" : 25 * mm});
        }
    });
